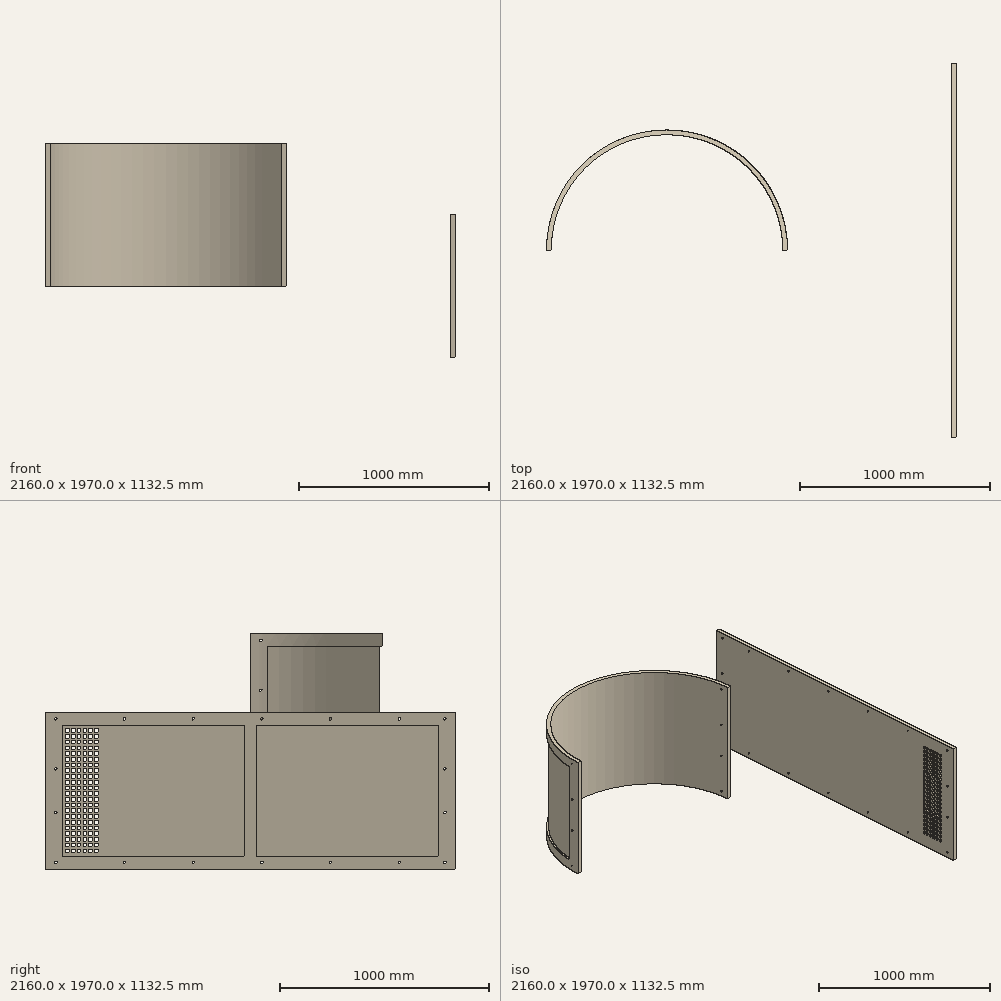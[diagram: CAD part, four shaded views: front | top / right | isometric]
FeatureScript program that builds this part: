
annotation { "Feature Type Name" : "Feature", "Feature Type Description" : "" }
export const myFeature = defineFeature(function(context is Context, id is Id, definition is map)
    precondition{}
    {
        {
            var Q0;
            Q0=qCreatedBy(makeId("Top.planeOp"),FACE);
            var sketch = newSketch(context, id + "F0", { "sketchPlane" : qUnion([Q0])});
            skArc(sketch, "E0", {"start": v(635, 0) * mm, "mid": v(0, 635) * mm, "end": v(-635, 0) * mm});
            skArc(sketch, "E1", {"start": v(610, 0) * mm, "mid": v(0, 610) * mm, "end": v(-610, 0) * mm});
            skLineSegment(sketch, "E2", {"start": v(-635, 0) * mm, "end": v(-610, 0) * mm});
            skLineSegment(sketch, "E3", {"start": v(610, 0) * mm, "end": v(635, 0) * mm});
            skSolve(sketch);
        }
        {
            var Q0;
            Q0 = qSketchRegion(id + "F0", true);
            extrude(context, id + "F1", {"entities" : qUnion([Q0]), "depth" : 755 * mm, "offsetDistance" : 25 * mm});
        }
        {
            var Q0;
            Q0=qCreatedBy(makeId("Top.planeOp"),FACE);
            cPlane(context, id + "F2", {"entities" : qUnion([Q0]), "cplaneType" : CPlaneType.OFFSET, "offset" : 62 * mm, "width" : 150 * mm, "height" : 150 * mm});
        }
        {
            var Q0;
            Q0=qCreatedBy(id+"F2.planeOp",FACE);
            var sketch = newSketch(context, id + "F3", { "sketchPlane" : qUnion([Q0])});
            skArc(sketch, "E4", {"start": v(629.97, 79.79) * mm, "mid": v(0, 635) * mm, "end": v(-629.97, 79.79) * mm});
            skArc(sketch, "E5", {"start": v(617.57, 78.22) * mm, "mid": v(0, 622.5) * mm, "end": v(-617.57, 78.22) * mm});
            skLineSegment(sketch, "E6", {"start": v(-629.97, 79.79) * mm, "end": v(-617.57, 78.22) * mm});
            skLineSegment(sketch, "E7", {"start": v(617.57, 78.22) * mm, "end": v(629.97, 79.79) * mm});
            skSolve(sketch);
        }
        {
            var Q0;
            Q0 = qSketchRegion(id + "F3", true);
            extrude(context, id + "F4", {"entities" : qUnion([Q0]), "operationType" : NewBodyOperationType.REMOVE, "depth" : 631 * mm, "offsetDistance" : 25 * mm});
        }
        {
            var Q0;
            Q0=qCreatedBy(makeId("Right.planeOp"),FACE);
            var sketch = newSketch(context, id + "F5", { "sketchPlane" : qUnion([Q0])});
            skCircle(sketch, "E8", {"center": v(50, 32.5) * mm, "radius": 6 * mm});
            skLineSegment(sketch, "E9", {"start": v(50, 32.5) * mm, "end": v(50, 272.5) * mm, "construction": true});
            skLineSegment(sketch, "E10", {"start": v(50, 272.5) * mm, "end": v(50, 482.5) * mm, "construction": true});
            skLineSegment(sketch, "E11", {"start": v(50, 482.5) * mm, "end": v(50, 722.5) * mm, "construction": true});
            skCircle(sketch, "E12", {"center": v(50, 722.5) * mm, "radius": 6 * mm});
            skCircle(sketch, "E13", {"center": v(50, 482.5) * mm, "radius": 6 * mm});
            skCircle(sketch, "E14", {"center": v(50, 272.5) * mm, "radius": 6 * mm});
            skSolve(sketch);
        }
        {
            var Q0;
            Q0 = qSketchRegion(id + "F5", true);
            extrude(context, id + "F6", {"entities" : qUnion([Q0]), "operationType" : NewBodyOperationType.REMOVE, "endBound" : BoundingType.THROUGH_ALL, "oppositeDirection" : true, "depth" : 25 * mm, "offsetDistance" : 25 * mm, "hasSecondDirection" : true, "secondDirectionBound" : BoundingType.THROUGH_ALL, "secondDirectionOppositeDirection" : false, "secondDirectionDepth" : 25 * mm});
        }
        {
            var Q0;
            Q0=qCreatedBy(makeId("Top.planeOp"),FACE);
            var sketch = newSketch(context, id + "F7", { "sketchPlane" : qUnion([Q0])});
            skArc(sketch, "E15", {"start": v(635, 0) * mm, "mid": v(109.45, 625.5) * mm, "end": v(-597.27, 215.62) * mm});
            skSolve(sketch);
        }
        {
            var Q0;
            Q0=qCreatedBy(makeId("Right.planeOp"),FACE);
            var sketch = newSketch(context, id + "F8", { "sketchPlane" : qUnion([Q0])});
            skCircle(sketch, "E16", {"center": v(50, 32.5) * mm, "radius": 6 * mm});
            skLineSegment(sketch, "E17", {"start": v(50, 32.5) * mm, "end": v(50, 722.5) * mm, "construction": true});
            skCircle(sketch, "E18", {"center": v(50, 722.5) * mm, "radius": 6 * mm});
            skSolve(sketch);
        }
        {
            var Q0;
            Q0 = qSketchRegion(id + "F8", true);
            extrude(context, id + "F9", {"entities" : qUnion([Q0]), "operationType" : NewBodyOperationType.REMOVE, "endBound" : BoundingType.THROUGH_ALL, "oppositeDirection" : true, "depth" : 25 * mm, "offsetDistance" : 25 * mm, "hasSecondDirection" : true, "secondDirectionBound" : BoundingType.THROUGH_ALL, "secondDirectionOppositeDirection" : false, "secondDirectionDepth" : 25 * mm});
        }
        {
            var Q0;
            Q0=qCreatedBy(makeId("Right.planeOp"),FACE);
            cPlane(context, id + "F10", {"entities" : qUnion([Q0]), "cplaneType" : CPlaneType.OFFSET, "offset" : 1500 * mm, "width" : 150 * mm, "height" : 150 * mm});
        }
        {
            var Q0;
            Q0=qCreatedBy(id+"F10.planeOp",FACE);
            var sketch = newSketch(context, id + "F11", { "sketchPlane" : qUnion([Q0])});
            skLineSegment(sketch, "E19.bottom", {"start": v(985, 377.5) * mm, "end": v(-985, 377.5) * mm});
            skLineSegment(sketch, "E19.top", {"start": v(985, -377.5) * mm, "end": v(-985, -377.5) * mm});
            skLineSegment(sketch, "E19.left", {"start": v(985, 377.5) * mm, "end": v(985, -377.5) * mm});
            skLineSegment(sketch, "E19.right", {"start": v(-985, 377.5) * mm, "end": v(-985, -377.5) * mm});
            skPoint(sketch, "E19.middle", {"position": v(0, 0) * mm});
            skCircle(sketch, "E20", {"center": v(-935, 345) * mm, "radius": 6 * mm});
            skCircle(sketch, "E21", {"center": v(-605, 345) * mm, "radius": 6 * mm});
            skCircle(sketch, "E22", {"center": v(-275, 345) * mm, "radius": 6 * mm});
            skCircle(sketch, "E23", {"center": v(55, 345) * mm, "radius": 6 * mm});
            skCircle(sketch, "E24", {"center": v(385, 345) * mm, "radius": 6 * mm});
            skCircle(sketch, "E25", {"center": v(715, 345) * mm, "radius": 6 * mm});
            skCircle(sketch, "E26", {"center": v(935, 345) * mm, "radius": 6 * mm});
            skCircle(sketch, "E27", {"center": v(-935, 105) * mm, "radius": 6 * mm});
            skCircle(sketch, "E28", {"center": v(-935, -105) * mm, "radius": 6 * mm});
            skCircle(sketch, "E29", {"center": v(-935, -345) * mm, "radius": 6 * mm});
            skCircle(sketch, "E30.MirrorC", {"center": v(-275, -345) * mm, "radius": 6 * mm});
            skCircle(sketch, "E31.MirrorC", {"center": v(715, -345) * mm, "radius": 6 * mm});
            skCircle(sketch, "E32.MirrorC", {"center": v(-605, -345) * mm, "radius": 6 * mm});
            skCircle(sketch, "E33.MirrorC", {"center": v(385, -345) * mm, "radius": 6 * mm});
            skCircle(sketch, "E34.MirrorC", {"center": v(55, -345) * mm, "radius": 6 * mm});
            skCircle(sketch, "E35.MirrorC", {"center": v(935, -105) * mm, "radius": 6 * mm});
            skCircle(sketch, "E36.MirrorC", {"center": v(935, 105) * mm, "radius": 6 * mm});
            skCircle(sketch, "E37", {"center": v(935, -345) * mm, "radius": 6 * mm});
            skSolve(sketch);
        }
        {
            var Q0;
            Q0 = qSketchRegion(id + "F11", true);
            extrude(context, id + "F12", {"entities" : qUnion([Q0]), "depth" : 25 * mm, "offsetDistance" : 25 * mm});
        }
        {
            var Q0;
            Q0=makeQuery(id+"F12.opExtrude","CAP_FACE",FACE,{"disambiguationData":[OSD([sQuery(id+"F11.wireOp",EDGE,"E19.bottom"),sQuery(id+"F11.wireOp",EDGE,"E19.left"),sQuery(id+"F11.wireOp",EDGE,"E19.right"),sQuery(id+"F11.wireOp",EDGE,"E20"),sQuery(id+"F11.wireOp",EDGE,"E21"),sQuery(id+"F11.wireOp",EDGE,"E22"),sQuery(id+"F11.wireOp",EDGE,"E23"),sQuery(id+"F11.wireOp",EDGE,"E24"),sQuery(id+"F11.wireOp",EDGE,"E25"),sQuery(id+"F11.wireOp",EDGE,"E26"),sQuery(id+"F11.wireOp",EDGE,"E27"),sQuery(id+"F11.wireOp",EDGE,"E28"),sQuery(id+"F11.wireOp",EDGE,"E29"),sQuery(id+"F11.wireOp",EDGE,"E30.MirrorC"),sQuery(id+"F11.wireOp",EDGE,"E31.MirrorC"),sQuery(id+"F11.wireOp",EDGE,"E32.MirrorC"),sQuery(id+"F11.wireOp",EDGE,"E33.MirrorC"),sQuery(id+"F11.wireOp",EDGE,"E34.MirrorC"),sQuery(id+"F11.wireOp",EDGE,"E19.top"),sQuery(id+"F11.wireOp",EDGE,"E35.MirrorC"),sQuery(id+"F11.wireOp",EDGE,"E36.MirrorC")])],"isStart":false});
            var sketch = newSketch(context, id + "F13", { "sketchPlane" : qUnion([Q0])});
            skLineSegment(sketch, "E38.left", {"start": v(905, 315.5) * mm, "end": v(905, -315.5) * mm});
            skLineSegment(sketch, "E38.right", {"start": v(-905, 315.5) * mm, "end": v(-905, -315.5) * mm});
            skPoint(sketch, "E38.middle", {"position": v(0, 0) * mm});
            skLineSegment(sketch, "E39", {"start": v(30, 315.5) * mm, "end": v(30, -315.5) * mm});
            skLineSegment(sketch, "E40", {"start": v(-30, 315.5) * mm, "end": v(-30, -315.5) * mm});
            skLineSegment(sketch, "E41", {"start": v(-905, -315.5) * mm, "end": v(-30, -315.5) * mm});
            skLineSegment(sketch, "E42", {"start": v(30, -315.5) * mm, "end": v(905, -315.5) * mm});
            skLineSegment(sketch, "E43", {"start": v(30, 315.5) * mm, "end": v(905, 315.5) * mm});
            skLineSegment(sketch, "E44", {"start": v(-905, 315.5) * mm, "end": v(-30, 315.5) * mm});
            skSolve(sketch);
        }
        {
            var Q0;
            Q0 = qSketchRegion(id + "F13", true);
            extrude(context, id + "F14", {"entities" : qUnion([Q0]), "operationType" : NewBodyOperationType.REMOVE, "oppositeDirection" : true, "depth" : 12.5 * mm, "offsetDistance" : 25 * mm});
        }
        {
            var Q0;
            Q0=makeQuery(id+"F14.boolean.opBoolean","COPY",FACE,{"derivedFrom":makeQuery(id+"F14.opExtrude","CAP_FACE",FACE,{"disambiguationData":[OSD([sQuery(id+"F13.wireOp",EDGE,"E38.right"),sQuery(id+"F13.wireOp",EDGE,"E40"),sQuery(id+"F13.wireOp",EDGE,"E41"),sQuery(id+"F13.wireOp",EDGE,"E44")])],"isStart":false})});
            var sketch = newSketch(context, id + "F15", { "sketchPlane" : qUnion([Q0])});
            skLineSegment(sketch, "E45.bottom", {"start": v(-887, 297.5) * mm, "end": v(-869.5, 297.5) * mm});
            skLineSegment(sketch, "E45.top", {"start": v(-887, 280) * mm, "end": v(-869.5, 280) * mm});
            skLineSegment(sketch, "E45.left", {"start": v(-887, 297.5) * mm, "end": v(-887, 280) * mm});
            skLineSegment(sketch, "E45.right", {"start": v(-869.5, 297.5) * mm, "end": v(-869.5, 280) * mm});
            skLineSegment(sketch, "E46.top", {"start": v(-887, 315.5) * mm, "end": v(-905, 315.5) * mm});
            skLineSegment(sketch, "E46.left", {"start": v(-887, 297.5) * mm, "end": v(-887, 315.5) * mm});
            skLineSegment(sketch, "E46.right", {"start": v(-905, 281.18) * mm, "end": v(-905, 315.5) * mm});
            skLineSegment(sketch, "E47.0.1.0", {"start": v(-869.5, 270) * mm, "end": v(-869.5, 252.5) * mm});
            skLineSegment(sketch, "E47.0.1.1", {"start": v(-887, 270) * mm, "end": v(-887, 288) * mm});
            skLineSegment(sketch, "E47.0.1.2", {"start": v(-887, 270) * mm, "end": v(-869.5, 270) * mm});
            skLineSegment(sketch, "E47.0.1.3", {"start": v(-887, 252.5) * mm, "end": v(-869.5, 252.5) * mm});
            skLineSegment(sketch, "E47.0.1.4", {"start": v(-887, 270) * mm, "end": v(-887, 252.5) * mm});
            skLineSegment(sketch, "E47.0.2.0", {"start": v(-869.5, 242.5) * mm, "end": v(-869.5, 225) * mm});
            skLineSegment(sketch, "E47.0.2.1", {"start": v(-887, 242.5) * mm, "end": v(-887, 260.5) * mm});
            skLineSegment(sketch, "E47.0.2.2", {"start": v(-887, 242.5) * mm, "end": v(-869.5, 242.5) * mm});
            skLineSegment(sketch, "E47.0.2.3", {"start": v(-887, 225) * mm, "end": v(-869.5, 225) * mm});
            skLineSegment(sketch, "E47.0.2.4", {"start": v(-887, 242.5) * mm, "end": v(-887, 225) * mm});
            skLineSegment(sketch, "E47.0.3.0", {"start": v(-869.5, 215) * mm, "end": v(-869.5, 197.5) * mm});
            skLineSegment(sketch, "E47.0.3.1", {"start": v(-887, 215) * mm, "end": v(-887, 233) * mm});
            skLineSegment(sketch, "E47.0.3.2", {"start": v(-887, 215) * mm, "end": v(-869.5, 215) * mm});
            skLineSegment(sketch, "E47.0.3.3", {"start": v(-887, 197.5) * mm, "end": v(-869.5, 197.5) * mm});
            skLineSegment(sketch, "E47.0.3.4", {"start": v(-887, 215) * mm, "end": v(-887, 197.5) * mm});
            skLineSegment(sketch, "E47.0.4.0", {"start": v(-869.5, 187.5) * mm, "end": v(-869.5, 170) * mm});
            skLineSegment(sketch, "E47.0.4.1", {"start": v(-887, 187.5) * mm, "end": v(-887, 205.5) * mm});
            skLineSegment(sketch, "E47.0.4.2", {"start": v(-887, 187.5) * mm, "end": v(-869.5, 187.5) * mm});
            skLineSegment(sketch, "E47.0.4.3", {"start": v(-887, 170) * mm, "end": v(-869.5, 170) * mm});
            skLineSegment(sketch, "E47.0.4.4", {"start": v(-887, 187.5) * mm, "end": v(-887, 170) * mm});
            skLineSegment(sketch, "E47.0.5.0", {"start": v(-869.5, 160) * mm, "end": v(-869.5, 142.5) * mm});
            skLineSegment(sketch, "E47.0.5.1", {"start": v(-887, 160) * mm, "end": v(-887, 178) * mm});
            skLineSegment(sketch, "E47.0.5.2", {"start": v(-887, 160) * mm, "end": v(-869.5, 160) * mm});
            skLineSegment(sketch, "E47.0.5.3", {"start": v(-887, 142.5) * mm, "end": v(-869.5, 142.5) * mm});
            skLineSegment(sketch, "E47.0.5.4", {"start": v(-887, 160) * mm, "end": v(-887, 142.5) * mm});
            skLineSegment(sketch, "E47.1.0.0", {"start": v(-842, 297.5) * mm, "end": v(-842, 280) * mm});
            skLineSegment(sketch, "E47.1.0.1", {"start": v(-859.5, 297.5) * mm, "end": v(-859.5, 315.5) * mm});
            skLineSegment(sketch, "E47.1.0.2", {"start": v(-859.5, 297.5) * mm, "end": v(-842, 297.5) * mm});
            skLineSegment(sketch, "E47.1.0.3", {"start": v(-859.5, 280) * mm, "end": v(-842, 280) * mm});
            skLineSegment(sketch, "E47.1.0.4", {"start": v(-859.5, 297.5) * mm, "end": v(-859.5, 280) * mm});
            skLineSegment(sketch, "E47.1.1.0", {"start": v(-842, 270) * mm, "end": v(-842, 252.5) * mm});
            skLineSegment(sketch, "E47.1.1.1", {"start": v(-859.5, 270) * mm, "end": v(-859.5, 288) * mm});
            skLineSegment(sketch, "E47.1.1.2", {"start": v(-859.5, 270) * mm, "end": v(-842, 270) * mm});
            skLineSegment(sketch, "E47.1.1.3", {"start": v(-859.5, 252.5) * mm, "end": v(-842, 252.5) * mm});
            skLineSegment(sketch, "E47.1.1.4", {"start": v(-859.5, 270) * mm, "end": v(-859.5, 252.5) * mm});
            skLineSegment(sketch, "E47.1.2.0", {"start": v(-842, 242.5) * mm, "end": v(-842, 225) * mm});
            skLineSegment(sketch, "E47.1.2.1", {"start": v(-859.5, 242.5) * mm, "end": v(-859.5, 260.5) * mm});
            skLineSegment(sketch, "E47.1.2.2", {"start": v(-859.5, 242.5) * mm, "end": v(-842, 242.5) * mm});
            skLineSegment(sketch, "E47.1.2.3", {"start": v(-859.5, 225) * mm, "end": v(-842, 225) * mm});
            skLineSegment(sketch, "E47.1.2.4", {"start": v(-859.5, 242.5) * mm, "end": v(-859.5, 225) * mm});
            skLineSegment(sketch, "E47.1.3.0", {"start": v(-842, 215) * mm, "end": v(-842, 197.5) * mm});
            skLineSegment(sketch, "E47.1.3.1", {"start": v(-859.5, 215) * mm, "end": v(-859.5, 233) * mm});
            skLineSegment(sketch, "E47.1.3.2", {"start": v(-859.5, 215) * mm, "end": v(-842, 215) * mm});
            skLineSegment(sketch, "E47.1.3.3", {"start": v(-859.5, 197.5) * mm, "end": v(-842, 197.5) * mm});
            skLineSegment(sketch, "E47.1.3.4", {"start": v(-859.5, 215) * mm, "end": v(-859.5, 197.5) * mm});
            skLineSegment(sketch, "E47.1.4.0", {"start": v(-842, 187.5) * mm, "end": v(-842, 170) * mm});
            skLineSegment(sketch, "E47.1.4.1", {"start": v(-859.5, 187.5) * mm, "end": v(-859.5, 205.5) * mm});
            skLineSegment(sketch, "E47.1.4.2", {"start": v(-859.5, 187.5) * mm, "end": v(-842, 187.5) * mm});
            skLineSegment(sketch, "E47.1.4.3", {"start": v(-859.5, 170) * mm, "end": v(-842, 170) * mm});
            skLineSegment(sketch, "E47.1.4.4", {"start": v(-859.5, 187.5) * mm, "end": v(-859.5, 170) * mm});
            skLineSegment(sketch, "E47.1.5.0", {"start": v(-842, 160) * mm, "end": v(-842, 142.5) * mm});
            skLineSegment(sketch, "E47.1.5.1", {"start": v(-859.5, 160) * mm, "end": v(-859.5, 178) * mm});
            skLineSegment(sketch, "E47.1.5.2", {"start": v(-859.5, 160) * mm, "end": v(-842, 160) * mm});
            skLineSegment(sketch, "E47.1.5.3", {"start": v(-859.5, 142.5) * mm, "end": v(-842, 142.5) * mm});
            skLineSegment(sketch, "E47.1.5.4", {"start": v(-859.5, 160) * mm, "end": v(-859.5, 142.5) * mm});
            skLineSegment(sketch, "E47.2.0.0", {"start": v(-814.5, 297.5) * mm, "end": v(-814.5, 280) * mm});
            skLineSegment(sketch, "E47.2.0.1", {"start": v(-832, 297.5) * mm, "end": v(-832, 315.5) * mm});
            skLineSegment(sketch, "E47.2.0.2", {"start": v(-832, 297.5) * mm, "end": v(-814.5, 297.5) * mm});
            skLineSegment(sketch, "E47.2.0.3", {"start": v(-832, 280) * mm, "end": v(-814.5, 280) * mm});
            skLineSegment(sketch, "E47.2.0.4", {"start": v(-832, 297.5) * mm, "end": v(-832, 280) * mm});
            skLineSegment(sketch, "E47.2.1.0", {"start": v(-814.5, 270) * mm, "end": v(-814.5, 252.5) * mm});
            skLineSegment(sketch, "E47.2.1.1", {"start": v(-832, 270) * mm, "end": v(-832, 288) * mm});
            skLineSegment(sketch, "E47.2.1.2", {"start": v(-832, 270) * mm, "end": v(-814.5, 270) * mm});
            skLineSegment(sketch, "E47.2.1.3", {"start": v(-832, 252.5) * mm, "end": v(-814.5, 252.5) * mm});
            skLineSegment(sketch, "E47.2.1.4", {"start": v(-832, 270) * mm, "end": v(-832, 252.5) * mm});
            skLineSegment(sketch, "E47.2.2.0", {"start": v(-814.5, 242.5) * mm, "end": v(-814.5, 225) * mm});
            skLineSegment(sketch, "E47.2.2.1", {"start": v(-832, 242.5) * mm, "end": v(-832, 260.5) * mm});
            skLineSegment(sketch, "E47.2.2.2", {"start": v(-832, 242.5) * mm, "end": v(-814.5, 242.5) * mm});
            skLineSegment(sketch, "E47.2.2.3", {"start": v(-832, 225) * mm, "end": v(-814.5, 225) * mm});
            skLineSegment(sketch, "E47.2.2.4", {"start": v(-832, 242.5) * mm, "end": v(-832, 225) * mm});
            skLineSegment(sketch, "E47.2.3.0", {"start": v(-814.5, 215) * mm, "end": v(-814.5, 197.5) * mm});
            skLineSegment(sketch, "E47.2.3.1", {"start": v(-832, 215) * mm, "end": v(-832, 233) * mm});
            skLineSegment(sketch, "E47.2.3.2", {"start": v(-832, 215) * mm, "end": v(-814.5, 215) * mm});
            skLineSegment(sketch, "E47.2.3.3", {"start": v(-832, 197.5) * mm, "end": v(-814.5, 197.5) * mm});
            skLineSegment(sketch, "E47.2.3.4", {"start": v(-832, 215) * mm, "end": v(-832, 197.5) * mm});
            skLineSegment(sketch, "E47.2.4.0", {"start": v(-814.5, 187.5) * mm, "end": v(-814.5, 170) * mm});
            skLineSegment(sketch, "E47.2.4.1", {"start": v(-832, 187.5) * mm, "end": v(-832, 205.5) * mm});
            skLineSegment(sketch, "E47.2.4.2", {"start": v(-832, 187.5) * mm, "end": v(-814.5, 187.5) * mm});
            skLineSegment(sketch, "E47.2.4.3", {"start": v(-832, 170) * mm, "end": v(-814.5, 170) * mm});
            skLineSegment(sketch, "E47.2.4.4", {"start": v(-832, 187.5) * mm, "end": v(-832, 170) * mm});
            skLineSegment(sketch, "E47.2.5.0", {"start": v(-814.5, 160) * mm, "end": v(-814.5, 142.5) * mm});
            skLineSegment(sketch, "E47.2.5.1", {"start": v(-832, 160) * mm, "end": v(-832, 178) * mm});
            skLineSegment(sketch, "E47.2.5.2", {"start": v(-832, 160) * mm, "end": v(-814.5, 160) * mm});
            skLineSegment(sketch, "E47.2.5.3", {"start": v(-832, 142.5) * mm, "end": v(-814.5, 142.5) * mm});
            skLineSegment(sketch, "E47.2.5.4", {"start": v(-832, 160) * mm, "end": v(-832, 142.5) * mm});
            skLineSegment(sketch, "E47.3.0.0", {"start": v(-787, 297.5) * mm, "end": v(-787, 280) * mm});
            skLineSegment(sketch, "E47.3.0.1", {"start": v(-804.5, 297.5) * mm, "end": v(-804.5, 315.5) * mm});
            skLineSegment(sketch, "E47.3.0.2", {"start": v(-804.5, 297.5) * mm, "end": v(-787, 297.5) * mm});
            skLineSegment(sketch, "E47.3.0.3", {"start": v(-804.5, 280) * mm, "end": v(-787, 280) * mm});
            skLineSegment(sketch, "E47.3.0.4", {"start": v(-804.5, 297.5) * mm, "end": v(-804.5, 280) * mm});
            skLineSegment(sketch, "E47.3.1.0", {"start": v(-787, 270) * mm, "end": v(-787, 252.5) * mm});
            skLineSegment(sketch, "E47.3.1.1", {"start": v(-804.5, 270) * mm, "end": v(-804.5, 288) * mm});
            skLineSegment(sketch, "E47.3.1.2", {"start": v(-804.5, 270) * mm, "end": v(-787, 270) * mm});
            skLineSegment(sketch, "E47.3.1.3", {"start": v(-804.5, 252.5) * mm, "end": v(-787, 252.5) * mm});
            skLineSegment(sketch, "E47.3.1.4", {"start": v(-804.5, 270) * mm, "end": v(-804.5, 252.5) * mm});
            skLineSegment(sketch, "E47.3.2.0", {"start": v(-787, 242.5) * mm, "end": v(-787, 225) * mm});
            skLineSegment(sketch, "E47.3.2.1", {"start": v(-804.5, 242.5) * mm, "end": v(-804.5, 260.5) * mm});
            skLineSegment(sketch, "E47.3.2.2", {"start": v(-804.5, 242.5) * mm, "end": v(-787, 242.5) * mm});
            skLineSegment(sketch, "E47.3.2.3", {"start": v(-804.5, 225) * mm, "end": v(-787, 225) * mm});
            skLineSegment(sketch, "E47.3.2.4", {"start": v(-804.5, 242.5) * mm, "end": v(-804.5, 225) * mm});
            skLineSegment(sketch, "E47.3.3.0", {"start": v(-787, 215) * mm, "end": v(-787, 197.5) * mm});
            skLineSegment(sketch, "E47.3.3.1", {"start": v(-804.5, 215) * mm, "end": v(-804.5, 233) * mm});
            skLineSegment(sketch, "E47.3.3.2", {"start": v(-804.5, 215) * mm, "end": v(-787, 215) * mm});
            skLineSegment(sketch, "E47.3.3.3", {"start": v(-804.5, 197.5) * mm, "end": v(-787, 197.5) * mm});
            skLineSegment(sketch, "E47.3.3.4", {"start": v(-804.5, 215) * mm, "end": v(-804.5, 197.5) * mm});
            skLineSegment(sketch, "E47.3.4.0", {"start": v(-787, 187.5) * mm, "end": v(-787, 170) * mm});
            skLineSegment(sketch, "E47.3.4.1", {"start": v(-804.5, 187.5) * mm, "end": v(-804.5, 205.5) * mm});
            skLineSegment(sketch, "E47.3.4.2", {"start": v(-804.5, 187.5) * mm, "end": v(-787, 187.5) * mm});
            skLineSegment(sketch, "E47.3.4.3", {"start": v(-804.5, 170) * mm, "end": v(-787, 170) * mm});
            skLineSegment(sketch, "E47.3.4.4", {"start": v(-804.5, 187.5) * mm, "end": v(-804.5, 170) * mm});
            skLineSegment(sketch, "E47.3.5.0", {"start": v(-787, 160) * mm, "end": v(-787, 142.5) * mm});
            skLineSegment(sketch, "E47.3.5.1", {"start": v(-804.5, 160) * mm, "end": v(-804.5, 178) * mm});
            skLineSegment(sketch, "E47.3.5.2", {"start": v(-804.5, 160) * mm, "end": v(-787, 160) * mm});
            skLineSegment(sketch, "E47.3.5.3", {"start": v(-804.5, 142.5) * mm, "end": v(-787, 142.5) * mm});
            skLineSegment(sketch, "E47.3.5.4", {"start": v(-804.5, 160) * mm, "end": v(-804.5, 142.5) * mm});
            skLineSegment(sketch, "E47.4.0.0", {"start": v(-759.5, 297.5) * mm, "end": v(-759.5, 280) * mm});
            skLineSegment(sketch, "E47.4.0.1", {"start": v(-777, 297.5) * mm, "end": v(-777, 315.5) * mm});
            skLineSegment(sketch, "E47.4.0.2", {"start": v(-777, 297.5) * mm, "end": v(-759.5, 297.5) * mm});
            skLineSegment(sketch, "E47.4.0.3", {"start": v(-777, 280) * mm, "end": v(-759.5, 280) * mm});
            skLineSegment(sketch, "E47.4.0.4", {"start": v(-777, 297.5) * mm, "end": v(-777, 280) * mm});
            skLineSegment(sketch, "E47.4.1.0", {"start": v(-759.5, 270) * mm, "end": v(-759.5, 252.5) * mm});
            skLineSegment(sketch, "E47.4.1.1", {"start": v(-777, 270) * mm, "end": v(-777, 288) * mm});
            skLineSegment(sketch, "E47.4.1.2", {"start": v(-777, 270) * mm, "end": v(-759.5, 270) * mm});
            skLineSegment(sketch, "E47.4.1.3", {"start": v(-777, 252.5) * mm, "end": v(-759.5, 252.5) * mm});
            skLineSegment(sketch, "E47.4.1.4", {"start": v(-777, 270) * mm, "end": v(-777, 252.5) * mm});
            skLineSegment(sketch, "E47.4.2.0", {"start": v(-759.5, 242.5) * mm, "end": v(-759.5, 225) * mm});
            skLineSegment(sketch, "E47.4.2.1", {"start": v(-777, 242.5) * mm, "end": v(-777, 260.5) * mm});
            skLineSegment(sketch, "E47.4.2.2", {"start": v(-777, 242.5) * mm, "end": v(-759.5, 242.5) * mm});
            skLineSegment(sketch, "E47.4.2.3", {"start": v(-777, 225) * mm, "end": v(-759.5, 225) * mm});
            skLineSegment(sketch, "E47.4.2.4", {"start": v(-777, 242.5) * mm, "end": v(-777, 225) * mm});
            skLineSegment(sketch, "E47.4.3.0", {"start": v(-759.5, 215) * mm, "end": v(-759.5, 197.5) * mm});
            skLineSegment(sketch, "E47.4.3.1", {"start": v(-777, 215) * mm, "end": v(-777, 233) * mm});
            skLineSegment(sketch, "E47.4.3.2", {"start": v(-777, 215) * mm, "end": v(-759.5, 215) * mm});
            skLineSegment(sketch, "E47.4.3.3", {"start": v(-777, 197.5) * mm, "end": v(-759.5, 197.5) * mm});
            skLineSegment(sketch, "E47.4.3.4", {"start": v(-777, 215) * mm, "end": v(-777, 197.5) * mm});
            skLineSegment(sketch, "E47.4.4.0", {"start": v(-759.5, 187.5) * mm, "end": v(-759.5, 170) * mm});
            skLineSegment(sketch, "E47.4.4.1", {"start": v(-777, 187.5) * mm, "end": v(-777, 205.5) * mm});
            skLineSegment(sketch, "E47.4.4.2", {"start": v(-777, 187.5) * mm, "end": v(-759.5, 187.5) * mm});
            skLineSegment(sketch, "E47.4.4.3", {"start": v(-777, 170) * mm, "end": v(-759.5, 170) * mm});
            skLineSegment(sketch, "E47.4.4.4", {"start": v(-777, 187.5) * mm, "end": v(-777, 170) * mm});
            skLineSegment(sketch, "E47.4.5.0", {"start": v(-759.5, 160) * mm, "end": v(-759.5, 142.5) * mm});
            skLineSegment(sketch, "E47.4.5.1", {"start": v(-777, 160) * mm, "end": v(-777, 178) * mm});
            skLineSegment(sketch, "E47.4.5.2", {"start": v(-777, 160) * mm, "end": v(-759.5, 160) * mm});
            skLineSegment(sketch, "E47.4.5.3", {"start": v(-777, 142.5) * mm, "end": v(-759.5, 142.5) * mm});
            skLineSegment(sketch, "E47.4.5.4", {"start": v(-777, 160) * mm, "end": v(-777, 142.5) * mm});
            skLineSegment(sketch, "E47.5.0.0", {"start": v(-732, 297.5) * mm, "end": v(-732, 280) * mm});
            skLineSegment(sketch, "E47.5.0.1", {"start": v(-749.5, 297.5) * mm, "end": v(-749.5, 315.5) * mm});
            skLineSegment(sketch, "E47.5.0.2", {"start": v(-749.5, 297.5) * mm, "end": v(-732, 297.5) * mm});
            skLineSegment(sketch, "E47.5.0.3", {"start": v(-749.5, 280) * mm, "end": v(-732, 280) * mm});
            skLineSegment(sketch, "E47.5.0.4", {"start": v(-749.5, 297.5) * mm, "end": v(-749.5, 280) * mm});
            skLineSegment(sketch, "E47.5.1.0", {"start": v(-732, 270) * mm, "end": v(-732, 252.5) * mm});
            skLineSegment(sketch, "E47.5.1.1", {"start": v(-749.5, 270) * mm, "end": v(-749.5, 288) * mm});
            skLineSegment(sketch, "E47.5.1.2", {"start": v(-749.5, 270) * mm, "end": v(-732, 270) * mm});
            skLineSegment(sketch, "E47.5.1.3", {"start": v(-749.5, 252.5) * mm, "end": v(-732, 252.5) * mm});
            skLineSegment(sketch, "E47.5.1.4", {"start": v(-749.5, 270) * mm, "end": v(-749.5, 252.5) * mm});
            skLineSegment(sketch, "E47.5.2.0", {"start": v(-732, 242.5) * mm, "end": v(-732, 225) * mm});
            skLineSegment(sketch, "E47.5.2.1", {"start": v(-749.5, 242.5) * mm, "end": v(-749.5, 260.5) * mm});
            skLineSegment(sketch, "E47.5.2.2", {"start": v(-749.5, 242.5) * mm, "end": v(-732, 242.5) * mm});
            skLineSegment(sketch, "E47.5.2.3", {"start": v(-749.5, 225) * mm, "end": v(-732, 225) * mm});
            skLineSegment(sketch, "E47.5.2.4", {"start": v(-749.5, 242.5) * mm, "end": v(-749.5, 225) * mm});
            skLineSegment(sketch, "E47.5.3.0", {"start": v(-732, 215) * mm, "end": v(-732, 197.5) * mm});
            skLineSegment(sketch, "E47.5.3.1", {"start": v(-749.5, 215) * mm, "end": v(-749.5, 233) * mm});
            skLineSegment(sketch, "E47.5.3.2", {"start": v(-749.5, 215) * mm, "end": v(-732, 215) * mm});
            skLineSegment(sketch, "E47.5.3.3", {"start": v(-749.5, 197.5) * mm, "end": v(-732, 197.5) * mm});
            skLineSegment(sketch, "E47.5.3.4", {"start": v(-749.5, 215) * mm, "end": v(-749.5, 197.5) * mm});
            skLineSegment(sketch, "E47.5.4.0", {"start": v(-732, 187.5) * mm, "end": v(-732, 170) * mm});
            skLineSegment(sketch, "E47.5.4.1", {"start": v(-749.5, 187.5) * mm, "end": v(-749.5, 205.5) * mm});
            skLineSegment(sketch, "E47.5.4.2", {"start": v(-749.5, 187.5) * mm, "end": v(-732, 187.5) * mm});
            skLineSegment(sketch, "E47.5.4.3", {"start": v(-749.5, 170) * mm, "end": v(-732, 170) * mm});
            skLineSegment(sketch, "E47.5.4.4", {"start": v(-749.5, 187.5) * mm, "end": v(-749.5, 170) * mm});
            skLineSegment(sketch, "E47.5.5.0", {"start": v(-732, 160) * mm, "end": v(-732, 142.5) * mm});
            skLineSegment(sketch, "E47.5.5.1", {"start": v(-749.5, 160) * mm, "end": v(-749.5, 178) * mm});
            skLineSegment(sketch, "E47.5.5.2", {"start": v(-749.5, 160) * mm, "end": v(-732, 160) * mm});
            skLineSegment(sketch, "E47.5.5.3", {"start": v(-749.5, 142.5) * mm, "end": v(-732, 142.5) * mm});
            skLineSegment(sketch, "E47.5.5.4", {"start": v(-749.5, 160) * mm, "end": v(-749.5, 142.5) * mm});
            skLineSegment(sketch, "E47.direction1", {"start": v(-887, 280) * mm, "end": v(-859.5, 280) * mm, "construction": true});
            skLineSegment(sketch, "E47.direction2", {"start": v(-887, 280) * mm, "end": v(-887, 252.5) * mm, "construction": true});
            skLineSegment(sketch, "E48.0.0.6", {"start": v(-869.5, 132.5) * mm, "end": v(-869.5, 115) * mm});
            skLineSegment(sketch, "E48.3.0.6", {"start": v(-887, 132.5) * mm, "end": v(-887, 150.5) * mm});
            skLineSegment(sketch, "E48.6.0.6", {"start": v(-887, 132.5) * mm, "end": v(-869.5, 132.5) * mm});
            skLineSegment(sketch, "E48.9.0.6", {"start": v(-887, 115) * mm, "end": v(-869.5, 115) * mm});
            skLineSegment(sketch, "E48.12.0.6", {"start": v(-887, 132.5) * mm, "end": v(-887, 115) * mm});
            skLineSegment(sketch, "E48.0.0.7", {"start": v(-869.5, 105) * mm, "end": v(-869.5, 87.5) * mm});
            skLineSegment(sketch, "E48.3.0.7", {"start": v(-887, 105) * mm, "end": v(-887, 123) * mm});
            skLineSegment(sketch, "E48.6.0.7", {"start": v(-887, 105) * mm, "end": v(-869.5, 105) * mm});
            skLineSegment(sketch, "E48.9.0.7", {"start": v(-887, 87.5) * mm, "end": v(-869.5, 87.5) * mm});
            skLineSegment(sketch, "E48.12.0.7", {"start": v(-887, 105) * mm, "end": v(-887, 87.5) * mm});
            skLineSegment(sketch, "E48.0.0.8", {"start": v(-869.5, 77.5) * mm, "end": v(-869.5, 60) * mm});
            skLineSegment(sketch, "E48.3.0.8", {"start": v(-887, 77.5) * mm, "end": v(-887, 95.5) * mm});
            skLineSegment(sketch, "E48.6.0.8", {"start": v(-887, 77.5) * mm, "end": v(-869.5, 77.5) * mm});
            skLineSegment(sketch, "E48.9.0.8", {"start": v(-887, 60) * mm, "end": v(-869.5, 60) * mm});
            skLineSegment(sketch, "E48.12.0.8", {"start": v(-887, 77.5) * mm, "end": v(-887, 60) * mm});
            skLineSegment(sketch, "E48.0.0.9", {"start": v(-869.5, 50) * mm, "end": v(-869.5, 32.5) * mm});
            skLineSegment(sketch, "E48.3.0.9", {"start": v(-887, 50) * mm, "end": v(-887, 68) * mm});
            skLineSegment(sketch, "E48.6.0.9", {"start": v(-887, 50) * mm, "end": v(-869.5, 50) * mm});
            skLineSegment(sketch, "E48.9.0.9", {"start": v(-887, 32.5) * mm, "end": v(-869.5, 32.5) * mm});
            skLineSegment(sketch, "E48.12.0.9", {"start": v(-887, 50) * mm, "end": v(-887, 32.5) * mm});
            skLineSegment(sketch, "E48.0.0.10", {"start": v(-869.5, 22.5) * mm, "end": v(-869.5, 5) * mm});
            skLineSegment(sketch, "E48.3.0.10", {"start": v(-887, 22.5) * mm, "end": v(-887, 40.5) * mm});
            skLineSegment(sketch, "E48.6.0.10", {"start": v(-887, 22.5) * mm, "end": v(-869.5, 22.5) * mm});
            skLineSegment(sketch, "E48.9.0.10", {"start": v(-887, 5) * mm, "end": v(-869.5, 5) * mm});
            skLineSegment(sketch, "E48.12.0.10", {"start": v(-887, 22.5) * mm, "end": v(-887, 5) * mm});
            skLineSegment(sketch, "E48.0.0.11", {"start": v(-869.5, -5) * mm, "end": v(-869.5, -22.5) * mm});
            skLineSegment(sketch, "E48.3.0.11", {"start": v(-887, -5) * mm, "end": v(-887, 13) * mm});
            skLineSegment(sketch, "E48.6.0.11", {"start": v(-887, -5) * mm, "end": v(-869.5, -5) * mm});
            skLineSegment(sketch, "E48.9.0.11", {"start": v(-887, -22.5) * mm, "end": v(-869.5, -22.5) * mm});
            skLineSegment(sketch, "E48.12.0.11", {"start": v(-887, -5) * mm, "end": v(-887, -22.5) * mm});
            skLineSegment(sketch, "E48.0.0.12", {"start": v(-869.5, -32.5) * mm, "end": v(-869.5, -50) * mm});
            skLineSegment(sketch, "E48.3.0.12", {"start": v(-887, -32.5) * mm, "end": v(-887, -14.5) * mm});
            skLineSegment(sketch, "E48.6.0.12", {"start": v(-887, -32.5) * mm, "end": v(-869.5, -32.5) * mm});
            skLineSegment(sketch, "E48.9.0.12", {"start": v(-887, -50) * mm, "end": v(-869.5, -50) * mm});
            skLineSegment(sketch, "E48.12.0.12", {"start": v(-887, -32.5) * mm, "end": v(-887, -50) * mm});
            skLineSegment(sketch, "E48.0.0.13", {"start": v(-869.5, -60) * mm, "end": v(-869.5, -77.5) * mm});
            skLineSegment(sketch, "E48.3.0.13", {"start": v(-887, -60) * mm, "end": v(-887, -42) * mm});
            skLineSegment(sketch, "E48.6.0.13", {"start": v(-887, -60) * mm, "end": v(-869.5, -60) * mm});
            skLineSegment(sketch, "E48.9.0.13", {"start": v(-887, -77.5) * mm, "end": v(-869.5, -77.5) * mm});
            skLineSegment(sketch, "E48.12.0.13", {"start": v(-887, -60) * mm, "end": v(-887, -77.5) * mm});
            skLineSegment(sketch, "E48.0.0.14", {"start": v(-869.5, -87.5) * mm, "end": v(-869.5, -105) * mm});
            skLineSegment(sketch, "E48.3.0.14", {"start": v(-887, -87.5) * mm, "end": v(-887, -69.5) * mm});
            skLineSegment(sketch, "E48.6.0.14", {"start": v(-887, -87.5) * mm, "end": v(-869.5, -87.5) * mm});
            skLineSegment(sketch, "E48.9.0.14", {"start": v(-887, -105) * mm, "end": v(-869.5, -105) * mm});
            skLineSegment(sketch, "E48.12.0.14", {"start": v(-887, -87.5) * mm, "end": v(-887, -105) * mm});
            skLineSegment(sketch, "E48.0.0.15", {"start": v(-869.5, -115) * mm, "end": v(-869.5, -132.5) * mm});
            skLineSegment(sketch, "E48.3.0.15", {"start": v(-887, -115) * mm, "end": v(-887, -97) * mm});
            skLineSegment(sketch, "E48.6.0.15", {"start": v(-887, -115) * mm, "end": v(-869.5, -115) * mm});
            skLineSegment(sketch, "E48.9.0.15", {"start": v(-887, -132.5) * mm, "end": v(-869.5, -132.5) * mm});
            skLineSegment(sketch, "E48.12.0.15", {"start": v(-887, -115) * mm, "end": v(-887, -132.5) * mm});
            skLineSegment(sketch, "E48.0.0.16", {"start": v(-869.5, -142.5) * mm, "end": v(-869.5, -160) * mm});
            skLineSegment(sketch, "E48.3.0.16", {"start": v(-887, -142.5) * mm, "end": v(-887, -124.5) * mm});
            skLineSegment(sketch, "E48.6.0.16", {"start": v(-887, -142.5) * mm, "end": v(-869.5, -142.5) * mm});
            skLineSegment(sketch, "E48.9.0.16", {"start": v(-887, -160) * mm, "end": v(-869.5, -160) * mm});
            skLineSegment(sketch, "E48.12.0.16", {"start": v(-887, -142.5) * mm, "end": v(-887, -160) * mm});
            skLineSegment(sketch, "E48.0.0.17", {"start": v(-869.5, -170) * mm, "end": v(-869.5, -187.5) * mm});
            skLineSegment(sketch, "E48.3.0.17", {"start": v(-887, -170) * mm, "end": v(-887, -152) * mm});
            skLineSegment(sketch, "E48.6.0.17", {"start": v(-887, -170) * mm, "end": v(-869.5, -170) * mm});
            skLineSegment(sketch, "E48.9.0.17", {"start": v(-887, -187.5) * mm, "end": v(-869.5, -187.5) * mm});
            skLineSegment(sketch, "E48.12.0.17", {"start": v(-887, -170) * mm, "end": v(-887, -187.5) * mm});
            skLineSegment(sketch, "E48.0.0.18", {"start": v(-869.5, -197.5) * mm, "end": v(-869.5, -215) * mm});
            skLineSegment(sketch, "E48.3.0.18", {"start": v(-887, -197.5) * mm, "end": v(-887, -179.5) * mm});
            skLineSegment(sketch, "E48.6.0.18", {"start": v(-887, -197.5) * mm, "end": v(-869.5, -197.5) * mm});
            skLineSegment(sketch, "E48.9.0.18", {"start": v(-887, -215) * mm, "end": v(-869.5, -215) * mm});
            skLineSegment(sketch, "E48.12.0.18", {"start": v(-887, -197.5) * mm, "end": v(-887, -215) * mm});
            skLineSegment(sketch, "E48.0.0.19", {"start": v(-869.5, -225) * mm, "end": v(-869.5, -242.5) * mm});
            skLineSegment(sketch, "E48.3.0.19", {"start": v(-887, -225) * mm, "end": v(-887, -207) * mm});
            skLineSegment(sketch, "E48.6.0.19", {"start": v(-887, -225) * mm, "end": v(-869.5, -225) * mm});
            skLineSegment(sketch, "E48.9.0.19", {"start": v(-887, -242.5) * mm, "end": v(-869.5, -242.5) * mm});
            skLineSegment(sketch, "E48.12.0.19", {"start": v(-887, -225) * mm, "end": v(-887, -242.5) * mm});
            skLineSegment(sketch, "E48.0.0.20", {"start": v(-869.5, -252.5) * mm, "end": v(-869.5, -270) * mm});
            skLineSegment(sketch, "E48.3.0.20", {"start": v(-887, -252.5) * mm, "end": v(-887, -234.5) * mm});
            skLineSegment(sketch, "E48.6.0.20", {"start": v(-887, -252.5) * mm, "end": v(-869.5, -252.5) * mm});
            skLineSegment(sketch, "E48.9.0.20", {"start": v(-887, -270) * mm, "end": v(-869.5, -270) * mm});
            skLineSegment(sketch, "E48.12.0.20", {"start": v(-887, -252.5) * mm, "end": v(-887, -270) * mm});
            skLineSegment(sketch, "E48.0.0.21", {"start": v(-869.5, -280) * mm, "end": v(-869.5, -297.5) * mm});
            skLineSegment(sketch, "E48.3.0.21", {"start": v(-887, -280) * mm, "end": v(-887, -262) * mm});
            skLineSegment(sketch, "E48.6.0.21", {"start": v(-887, -280) * mm, "end": v(-869.5, -280) * mm});
            skLineSegment(sketch, "E48.9.0.21", {"start": v(-887, -297.5) * mm, "end": v(-869.5, -297.5) * mm});
            skLineSegment(sketch, "E48.12.0.21", {"start": v(-887, -280) * mm, "end": v(-887, -297.5) * mm});
            skLineSegment(sketch, "E48.0.1.6", {"start": v(-842, 132.5) * mm, "end": v(-842, 115) * mm});
            skLineSegment(sketch, "E48.3.1.6", {"start": v(-859.5, 132.5) * mm, "end": v(-859.5, 150.5) * mm});
            skLineSegment(sketch, "E48.6.1.6", {"start": v(-859.5, 132.5) * mm, "end": v(-842, 132.5) * mm});
            skLineSegment(sketch, "E48.9.1.6", {"start": v(-859.5, 115) * mm, "end": v(-842, 115) * mm});
            skLineSegment(sketch, "E48.12.1.6", {"start": v(-859.5, 132.5) * mm, "end": v(-859.5, 115) * mm});
            skLineSegment(sketch, "E48.0.1.7", {"start": v(-842, 105) * mm, "end": v(-842, 87.5) * mm});
            skLineSegment(sketch, "E48.3.1.7", {"start": v(-859.5, 105) * mm, "end": v(-859.5, 123) * mm});
            skLineSegment(sketch, "E48.6.1.7", {"start": v(-859.5, 105) * mm, "end": v(-842, 105) * mm});
            skLineSegment(sketch, "E48.9.1.7", {"start": v(-859.5, 87.5) * mm, "end": v(-842, 87.5) * mm});
            skLineSegment(sketch, "E48.12.1.7", {"start": v(-859.5, 105) * mm, "end": v(-859.5, 87.5) * mm});
            skLineSegment(sketch, "E48.0.1.8", {"start": v(-842, 77.5) * mm, "end": v(-842, 60) * mm});
            skLineSegment(sketch, "E48.3.1.8", {"start": v(-859.5, 77.5) * mm, "end": v(-859.5, 95.5) * mm});
            skLineSegment(sketch, "E48.6.1.8", {"start": v(-859.5, 77.5) * mm, "end": v(-842, 77.5) * mm});
            skLineSegment(sketch, "E48.9.1.8", {"start": v(-859.5, 60) * mm, "end": v(-842, 60) * mm});
            skLineSegment(sketch, "E48.12.1.8", {"start": v(-859.5, 77.5) * mm, "end": v(-859.5, 60) * mm});
            skLineSegment(sketch, "E48.0.1.9", {"start": v(-842, 50) * mm, "end": v(-842, 32.5) * mm});
            skLineSegment(sketch, "E48.3.1.9", {"start": v(-859.5, 50) * mm, "end": v(-859.5, 68) * mm});
            skLineSegment(sketch, "E48.6.1.9", {"start": v(-859.5, 50) * mm, "end": v(-842, 50) * mm});
            skLineSegment(sketch, "E48.9.1.9", {"start": v(-859.5, 32.5) * mm, "end": v(-842, 32.5) * mm});
            skLineSegment(sketch, "E48.12.1.9", {"start": v(-859.5, 50) * mm, "end": v(-859.5, 32.5) * mm});
            skLineSegment(sketch, "E48.0.1.10", {"start": v(-842, 22.5) * mm, "end": v(-842, 5) * mm});
            skLineSegment(sketch, "E48.3.1.10", {"start": v(-859.5, 22.5) * mm, "end": v(-859.5, 40.5) * mm});
            skLineSegment(sketch, "E48.6.1.10", {"start": v(-859.5, 22.5) * mm, "end": v(-842, 22.5) * mm});
            skLineSegment(sketch, "E48.9.1.10", {"start": v(-859.5, 5) * mm, "end": v(-842, 5) * mm});
            skLineSegment(sketch, "E48.12.1.10", {"start": v(-859.5, 22.5) * mm, "end": v(-859.5, 5) * mm});
            skLineSegment(sketch, "E48.0.1.11", {"start": v(-842, -5) * mm, "end": v(-842, -22.5) * mm});
            skLineSegment(sketch, "E48.3.1.11", {"start": v(-859.5, -5) * mm, "end": v(-859.5, 13) * mm});
            skLineSegment(sketch, "E48.6.1.11", {"start": v(-859.5, -5) * mm, "end": v(-842, -5) * mm});
            skLineSegment(sketch, "E48.9.1.11", {"start": v(-859.5, -22.5) * mm, "end": v(-842, -22.5) * mm});
            skLineSegment(sketch, "E48.12.1.11", {"start": v(-859.5, -5) * mm, "end": v(-859.5, -22.5) * mm});
            skLineSegment(sketch, "E48.0.1.12", {"start": v(-842, -32.5) * mm, "end": v(-842, -50) * mm});
            skLineSegment(sketch, "E48.3.1.12", {"start": v(-859.5, -32.5) * mm, "end": v(-859.5, -14.5) * mm});
            skLineSegment(sketch, "E48.6.1.12", {"start": v(-859.5, -32.5) * mm, "end": v(-842, -32.5) * mm});
            skLineSegment(sketch, "E48.9.1.12", {"start": v(-859.5, -50) * mm, "end": v(-842, -50) * mm});
            skLineSegment(sketch, "E48.12.1.12", {"start": v(-859.5, -32.5) * mm, "end": v(-859.5, -50) * mm});
            skLineSegment(sketch, "E48.0.1.13", {"start": v(-842, -60) * mm, "end": v(-842, -77.5) * mm});
            skLineSegment(sketch, "E48.3.1.13", {"start": v(-859.5, -60) * mm, "end": v(-859.5, -42) * mm});
            skLineSegment(sketch, "E48.6.1.13", {"start": v(-859.5, -60) * mm, "end": v(-842, -60) * mm});
            skLineSegment(sketch, "E48.9.1.13", {"start": v(-859.5, -77.5) * mm, "end": v(-842, -77.5) * mm});
            skLineSegment(sketch, "E48.12.1.13", {"start": v(-859.5, -60) * mm, "end": v(-859.5, -77.5) * mm});
            skLineSegment(sketch, "E48.0.1.14", {"start": v(-842, -87.5) * mm, "end": v(-842, -105) * mm});
            skLineSegment(sketch, "E48.3.1.14", {"start": v(-859.5, -87.5) * mm, "end": v(-859.5, -69.5) * mm});
            skLineSegment(sketch, "E48.6.1.14", {"start": v(-859.5, -87.5) * mm, "end": v(-842, -87.5) * mm});
            skLineSegment(sketch, "E48.9.1.14", {"start": v(-859.5, -105) * mm, "end": v(-842, -105) * mm});
            skLineSegment(sketch, "E48.12.1.14", {"start": v(-859.5, -87.5) * mm, "end": v(-859.5, -105) * mm});
            skLineSegment(sketch, "E48.0.1.15", {"start": v(-842, -115) * mm, "end": v(-842, -132.5) * mm});
            skLineSegment(sketch, "E48.3.1.15", {"start": v(-859.5, -115) * mm, "end": v(-859.5, -97) * mm});
            skLineSegment(sketch, "E48.6.1.15", {"start": v(-859.5, -115) * mm, "end": v(-842, -115) * mm});
            skLineSegment(sketch, "E48.9.1.15", {"start": v(-859.5, -132.5) * mm, "end": v(-842, -132.5) * mm});
            skLineSegment(sketch, "E48.12.1.15", {"start": v(-859.5, -115) * mm, "end": v(-859.5, -132.5) * mm});
            skLineSegment(sketch, "E48.0.1.16", {"start": v(-842, -142.5) * mm, "end": v(-842, -160) * mm});
            skLineSegment(sketch, "E48.3.1.16", {"start": v(-859.5, -142.5) * mm, "end": v(-859.5, -124.5) * mm});
            skLineSegment(sketch, "E48.6.1.16", {"start": v(-859.5, -142.5) * mm, "end": v(-842, -142.5) * mm});
            skLineSegment(sketch, "E48.9.1.16", {"start": v(-859.5, -160) * mm, "end": v(-842, -160) * mm});
            skLineSegment(sketch, "E48.12.1.16", {"start": v(-859.5, -142.5) * mm, "end": v(-859.5, -160) * mm});
            skLineSegment(sketch, "E48.0.1.17", {"start": v(-842, -170) * mm, "end": v(-842, -187.5) * mm});
            skLineSegment(sketch, "E48.3.1.17", {"start": v(-859.5, -170) * mm, "end": v(-859.5, -152) * mm});
            skLineSegment(sketch, "E48.6.1.17", {"start": v(-859.5, -170) * mm, "end": v(-842, -170) * mm});
            skLineSegment(sketch, "E48.9.1.17", {"start": v(-859.5, -187.5) * mm, "end": v(-842, -187.5) * mm});
            skLineSegment(sketch, "E48.12.1.17", {"start": v(-859.5, -170) * mm, "end": v(-859.5, -187.5) * mm});
            skLineSegment(sketch, "E48.0.1.18", {"start": v(-842, -197.5) * mm, "end": v(-842, -215) * mm});
            skLineSegment(sketch, "E48.3.1.18", {"start": v(-859.5, -197.5) * mm, "end": v(-859.5, -179.5) * mm});
            skLineSegment(sketch, "E48.6.1.18", {"start": v(-859.5, -197.5) * mm, "end": v(-842, -197.5) * mm});
            skLineSegment(sketch, "E48.9.1.18", {"start": v(-859.5, -215) * mm, "end": v(-842, -215) * mm});
            skLineSegment(sketch, "E48.12.1.18", {"start": v(-859.5, -197.5) * mm, "end": v(-859.5, -215) * mm});
            skLineSegment(sketch, "E48.0.1.19", {"start": v(-842, -225) * mm, "end": v(-842, -242.5) * mm});
            skLineSegment(sketch, "E48.3.1.19", {"start": v(-859.5, -225) * mm, "end": v(-859.5, -207) * mm});
            skLineSegment(sketch, "E48.6.1.19", {"start": v(-859.5, -225) * mm, "end": v(-842, -225) * mm});
            skLineSegment(sketch, "E48.9.1.19", {"start": v(-859.5, -242.5) * mm, "end": v(-842, -242.5) * mm});
            skLineSegment(sketch, "E48.12.1.19", {"start": v(-859.5, -225) * mm, "end": v(-859.5, -242.5) * mm});
            skLineSegment(sketch, "E48.0.1.20", {"start": v(-842, -252.5) * mm, "end": v(-842, -270) * mm});
            skLineSegment(sketch, "E48.3.1.20", {"start": v(-859.5, -252.5) * mm, "end": v(-859.5, -234.5) * mm});
            skLineSegment(sketch, "E48.6.1.20", {"start": v(-859.5, -252.5) * mm, "end": v(-842, -252.5) * mm});
            skLineSegment(sketch, "E48.9.1.20", {"start": v(-859.5, -270) * mm, "end": v(-842, -270) * mm});
            skLineSegment(sketch, "E48.12.1.20", {"start": v(-859.5, -252.5) * mm, "end": v(-859.5, -270) * mm});
            skLineSegment(sketch, "E48.0.1.21", {"start": v(-842, -280) * mm, "end": v(-842, -297.5) * mm});
            skLineSegment(sketch, "E48.3.1.21", {"start": v(-859.5, -280) * mm, "end": v(-859.5, -262) * mm});
            skLineSegment(sketch, "E48.6.1.21", {"start": v(-859.5, -280) * mm, "end": v(-842, -280) * mm});
            skLineSegment(sketch, "E48.9.1.21", {"start": v(-859.5, -297.5) * mm, "end": v(-842, -297.5) * mm});
            skLineSegment(sketch, "E48.12.1.21", {"start": v(-859.5, -280) * mm, "end": v(-859.5, -297.5) * mm});
            skLineSegment(sketch, "E48.0.2.6", {"start": v(-814.5, 132.5) * mm, "end": v(-814.5, 115) * mm});
            skLineSegment(sketch, "E48.3.2.6", {"start": v(-832, 132.5) * mm, "end": v(-832, 150.5) * mm});
            skLineSegment(sketch, "E48.6.2.6", {"start": v(-832, 132.5) * mm, "end": v(-814.5, 132.5) * mm});
            skLineSegment(sketch, "E48.9.2.6", {"start": v(-832, 115) * mm, "end": v(-814.5, 115) * mm});
            skLineSegment(sketch, "E48.12.2.6", {"start": v(-832, 132.5) * mm, "end": v(-832, 115) * mm});
            skLineSegment(sketch, "E48.0.2.7", {"start": v(-814.5, 105) * mm, "end": v(-814.5, 87.5) * mm});
            skLineSegment(sketch, "E48.3.2.7", {"start": v(-832, 105) * mm, "end": v(-832, 123) * mm});
            skLineSegment(sketch, "E48.6.2.7", {"start": v(-832, 105) * mm, "end": v(-814.5, 105) * mm});
            skLineSegment(sketch, "E48.9.2.7", {"start": v(-832, 87.5) * mm, "end": v(-814.5, 87.5) * mm});
            skLineSegment(sketch, "E48.12.2.7", {"start": v(-832, 105) * mm, "end": v(-832, 87.5) * mm});
            skLineSegment(sketch, "E48.0.2.8", {"start": v(-814.5, 77.5) * mm, "end": v(-814.5, 60) * mm});
            skLineSegment(sketch, "E48.3.2.8", {"start": v(-832, 77.5) * mm, "end": v(-832, 95.5) * mm});
            skLineSegment(sketch, "E48.6.2.8", {"start": v(-832, 77.5) * mm, "end": v(-814.5, 77.5) * mm});
            skLineSegment(sketch, "E48.9.2.8", {"start": v(-832, 60) * mm, "end": v(-814.5, 60) * mm});
            skLineSegment(sketch, "E48.12.2.8", {"start": v(-832, 77.5) * mm, "end": v(-832, 60) * mm});
            skLineSegment(sketch, "E48.0.2.9", {"start": v(-814.5, 50) * mm, "end": v(-814.5, 32.5) * mm});
            skLineSegment(sketch, "E48.3.2.9", {"start": v(-832, 50) * mm, "end": v(-832, 68) * mm});
            skLineSegment(sketch, "E48.6.2.9", {"start": v(-832, 50) * mm, "end": v(-814.5, 50) * mm});
            skLineSegment(sketch, "E48.9.2.9", {"start": v(-832, 32.5) * mm, "end": v(-814.5, 32.5) * mm});
            skLineSegment(sketch, "E48.12.2.9", {"start": v(-832, 50) * mm, "end": v(-832, 32.5) * mm});
            skLineSegment(sketch, "E48.0.2.10", {"start": v(-814.5, 22.5) * mm, "end": v(-814.5, 5) * mm});
            skLineSegment(sketch, "E48.3.2.10", {"start": v(-832, 22.5) * mm, "end": v(-832, 40.5) * mm});
            skLineSegment(sketch, "E48.6.2.10", {"start": v(-832, 22.5) * mm, "end": v(-814.5, 22.5) * mm});
            skLineSegment(sketch, "E48.9.2.10", {"start": v(-832, 5) * mm, "end": v(-814.5, 5) * mm});
            skLineSegment(sketch, "E48.12.2.10", {"start": v(-832, 22.5) * mm, "end": v(-832, 5) * mm});
            skLineSegment(sketch, "E48.0.2.11", {"start": v(-814.5, -5) * mm, "end": v(-814.5, -22.5) * mm});
            skLineSegment(sketch, "E48.3.2.11", {"start": v(-832, -5) * mm, "end": v(-832, 13) * mm});
            skLineSegment(sketch, "E48.6.2.11", {"start": v(-832, -5) * mm, "end": v(-814.5, -5) * mm});
            skLineSegment(sketch, "E48.9.2.11", {"start": v(-832, -22.5) * mm, "end": v(-814.5, -22.5) * mm});
            skLineSegment(sketch, "E48.12.2.11", {"start": v(-832, -5) * mm, "end": v(-832, -22.5) * mm});
            skLineSegment(sketch, "E48.0.2.12", {"start": v(-814.5, -32.5) * mm, "end": v(-814.5, -50) * mm});
            skLineSegment(sketch, "E48.3.2.12", {"start": v(-832, -32.5) * mm, "end": v(-832, -14.5) * mm});
            skLineSegment(sketch, "E48.6.2.12", {"start": v(-832, -32.5) * mm, "end": v(-814.5, -32.5) * mm});
            skLineSegment(sketch, "E48.9.2.12", {"start": v(-832, -50) * mm, "end": v(-814.5, -50) * mm});
            skLineSegment(sketch, "E48.12.2.12", {"start": v(-832, -32.5) * mm, "end": v(-832, -50) * mm});
            skLineSegment(sketch, "E48.0.2.13", {"start": v(-814.5, -60) * mm, "end": v(-814.5, -77.5) * mm});
            skLineSegment(sketch, "E48.3.2.13", {"start": v(-832, -60) * mm, "end": v(-832, -42) * mm});
            skLineSegment(sketch, "E48.6.2.13", {"start": v(-832, -60) * mm, "end": v(-814.5, -60) * mm});
            skLineSegment(sketch, "E48.9.2.13", {"start": v(-832, -77.5) * mm, "end": v(-814.5, -77.5) * mm});
            skLineSegment(sketch, "E48.12.2.13", {"start": v(-832, -60) * mm, "end": v(-832, -77.5) * mm});
            skLineSegment(sketch, "E48.0.2.14", {"start": v(-814.5, -87.5) * mm, "end": v(-814.5, -105) * mm});
            skLineSegment(sketch, "E48.3.2.14", {"start": v(-832, -87.5) * mm, "end": v(-832, -69.5) * mm});
            skLineSegment(sketch, "E48.6.2.14", {"start": v(-832, -87.5) * mm, "end": v(-814.5, -87.5) * mm});
            skLineSegment(sketch, "E48.9.2.14", {"start": v(-832, -105) * mm, "end": v(-814.5, -105) * mm});
            skLineSegment(sketch, "E48.12.2.14", {"start": v(-832, -87.5) * mm, "end": v(-832, -105) * mm});
            skLineSegment(sketch, "E48.0.2.15", {"start": v(-814.5, -115) * mm, "end": v(-814.5, -132.5) * mm});
            skLineSegment(sketch, "E48.3.2.15", {"start": v(-832, -115) * mm, "end": v(-832, -97) * mm});
            skLineSegment(sketch, "E48.6.2.15", {"start": v(-832, -115) * mm, "end": v(-814.5, -115) * mm});
            skLineSegment(sketch, "E48.9.2.15", {"start": v(-832, -132.5) * mm, "end": v(-814.5, -132.5) * mm});
            skLineSegment(sketch, "E48.12.2.15", {"start": v(-832, -115) * mm, "end": v(-832, -132.5) * mm});
            skLineSegment(sketch, "E48.0.2.16", {"start": v(-814.5, -142.5) * mm, "end": v(-814.5, -160) * mm});
            skLineSegment(sketch, "E48.3.2.16", {"start": v(-832, -142.5) * mm, "end": v(-832, -124.5) * mm});
            skLineSegment(sketch, "E48.6.2.16", {"start": v(-832, -142.5) * mm, "end": v(-814.5, -142.5) * mm});
            skLineSegment(sketch, "E48.9.2.16", {"start": v(-832, -160) * mm, "end": v(-814.5, -160) * mm});
            skLineSegment(sketch, "E48.12.2.16", {"start": v(-832, -142.5) * mm, "end": v(-832, -160) * mm});
            skLineSegment(sketch, "E48.0.2.17", {"start": v(-814.5, -170) * mm, "end": v(-814.5, -187.5) * mm});
            skLineSegment(sketch, "E48.3.2.17", {"start": v(-832, -170) * mm, "end": v(-832, -152) * mm});
            skLineSegment(sketch, "E48.6.2.17", {"start": v(-832, -170) * mm, "end": v(-814.5, -170) * mm});
            skLineSegment(sketch, "E48.9.2.17", {"start": v(-832, -187.5) * mm, "end": v(-814.5, -187.5) * mm});
            skLineSegment(sketch, "E48.12.2.17", {"start": v(-832, -170) * mm, "end": v(-832, -187.5) * mm});
            skLineSegment(sketch, "E48.0.2.18", {"start": v(-814.5, -197.5) * mm, "end": v(-814.5, -215) * mm});
            skLineSegment(sketch, "E48.3.2.18", {"start": v(-832, -197.5) * mm, "end": v(-832, -179.5) * mm});
            skLineSegment(sketch, "E48.6.2.18", {"start": v(-832, -197.5) * mm, "end": v(-814.5, -197.5) * mm});
            skLineSegment(sketch, "E48.9.2.18", {"start": v(-832, -215) * mm, "end": v(-814.5, -215) * mm});
            skLineSegment(sketch, "E48.12.2.18", {"start": v(-832, -197.5) * mm, "end": v(-832, -215) * mm});
            skLineSegment(sketch, "E48.0.2.19", {"start": v(-814.5, -225) * mm, "end": v(-814.5, -242.5) * mm});
            skLineSegment(sketch, "E48.3.2.19", {"start": v(-832, -225) * mm, "end": v(-832, -207) * mm});
            skLineSegment(sketch, "E48.6.2.19", {"start": v(-832, -225) * mm, "end": v(-814.5, -225) * mm});
            skLineSegment(sketch, "E48.9.2.19", {"start": v(-832, -242.5) * mm, "end": v(-814.5, -242.5) * mm});
            skLineSegment(sketch, "E48.12.2.19", {"start": v(-832, -225) * mm, "end": v(-832, -242.5) * mm});
            skLineSegment(sketch, "E48.0.2.20", {"start": v(-814.5, -252.5) * mm, "end": v(-814.5, -270) * mm});
            skLineSegment(sketch, "E48.3.2.20", {"start": v(-832, -252.5) * mm, "end": v(-832, -234.5) * mm});
            skLineSegment(sketch, "E48.6.2.20", {"start": v(-832, -252.5) * mm, "end": v(-814.5, -252.5) * mm});
            skLineSegment(sketch, "E48.9.2.20", {"start": v(-832, -270) * mm, "end": v(-814.5, -270) * mm});
            skLineSegment(sketch, "E48.12.2.20", {"start": v(-832, -252.5) * mm, "end": v(-832, -270) * mm});
            skLineSegment(sketch, "E48.0.2.21", {"start": v(-814.5, -280) * mm, "end": v(-814.5, -297.5) * mm});
            skLineSegment(sketch, "E48.3.2.21", {"start": v(-832, -280) * mm, "end": v(-832, -262) * mm});
            skLineSegment(sketch, "E48.6.2.21", {"start": v(-832, -280) * mm, "end": v(-814.5, -280) * mm});
            skLineSegment(sketch, "E48.9.2.21", {"start": v(-832, -297.5) * mm, "end": v(-814.5, -297.5) * mm});
            skLineSegment(sketch, "E48.12.2.21", {"start": v(-832, -280) * mm, "end": v(-832, -297.5) * mm});
            skLineSegment(sketch, "E48.0.3.6", {"start": v(-787, 132.5) * mm, "end": v(-787, 115) * mm});
            skLineSegment(sketch, "E48.3.3.6", {"start": v(-804.5, 132.5) * mm, "end": v(-804.5, 150.5) * mm});
            skLineSegment(sketch, "E48.6.3.6", {"start": v(-804.5, 132.5) * mm, "end": v(-787, 132.5) * mm});
            skLineSegment(sketch, "E48.9.3.6", {"start": v(-804.5, 115) * mm, "end": v(-787, 115) * mm});
            skLineSegment(sketch, "E48.12.3.6", {"start": v(-804.5, 132.5) * mm, "end": v(-804.5, 115) * mm});
            skLineSegment(sketch, "E48.0.3.7", {"start": v(-787, 105) * mm, "end": v(-787, 87.5) * mm});
            skLineSegment(sketch, "E48.3.3.7", {"start": v(-804.5, 105) * mm, "end": v(-804.5, 123) * mm});
            skLineSegment(sketch, "E48.6.3.7", {"start": v(-804.5, 105) * mm, "end": v(-787, 105) * mm});
            skLineSegment(sketch, "E48.9.3.7", {"start": v(-804.5, 87.5) * mm, "end": v(-787, 87.5) * mm});
            skLineSegment(sketch, "E48.12.3.7", {"start": v(-804.5, 105) * mm, "end": v(-804.5, 87.5) * mm});
            skLineSegment(sketch, "E48.0.3.8", {"start": v(-787, 77.5) * mm, "end": v(-787, 60) * mm});
            skLineSegment(sketch, "E48.3.3.8", {"start": v(-804.5, 77.5) * mm, "end": v(-804.5, 95.5) * mm});
            skLineSegment(sketch, "E48.6.3.8", {"start": v(-804.5, 77.5) * mm, "end": v(-787, 77.5) * mm});
            skLineSegment(sketch, "E48.9.3.8", {"start": v(-804.5, 60) * mm, "end": v(-787, 60) * mm});
            skLineSegment(sketch, "E48.12.3.8", {"start": v(-804.5, 77.5) * mm, "end": v(-804.5, 60) * mm});
            skLineSegment(sketch, "E48.0.3.9", {"start": v(-787, 50) * mm, "end": v(-787, 32.5) * mm});
            skLineSegment(sketch, "E48.3.3.9", {"start": v(-804.5, 50) * mm, "end": v(-804.5, 68) * mm});
            skLineSegment(sketch, "E48.6.3.9", {"start": v(-804.5, 50) * mm, "end": v(-787, 50) * mm});
            skLineSegment(sketch, "E48.9.3.9", {"start": v(-804.5, 32.5) * mm, "end": v(-787, 32.5) * mm});
            skLineSegment(sketch, "E48.12.3.9", {"start": v(-804.5, 50) * mm, "end": v(-804.5, 32.5) * mm});
            skLineSegment(sketch, "E48.0.3.10", {"start": v(-787, 22.5) * mm, "end": v(-787, 5) * mm});
            skLineSegment(sketch, "E48.3.3.10", {"start": v(-804.5, 22.5) * mm, "end": v(-804.5, 40.5) * mm});
            skLineSegment(sketch, "E48.6.3.10", {"start": v(-804.5, 22.5) * mm, "end": v(-787, 22.5) * mm});
            skLineSegment(sketch, "E48.9.3.10", {"start": v(-804.5, 5) * mm, "end": v(-787, 5) * mm});
            skLineSegment(sketch, "E48.12.3.10", {"start": v(-804.5, 22.5) * mm, "end": v(-804.5, 5) * mm});
            skLineSegment(sketch, "E48.0.3.11", {"start": v(-787, -5) * mm, "end": v(-787, -22.5) * mm});
            skLineSegment(sketch, "E48.3.3.11", {"start": v(-804.5, -5) * mm, "end": v(-804.5, 13) * mm});
            skLineSegment(sketch, "E48.6.3.11", {"start": v(-804.5, -5) * mm, "end": v(-787, -5) * mm});
            skLineSegment(sketch, "E48.9.3.11", {"start": v(-804.5, -22.5) * mm, "end": v(-787, -22.5) * mm});
            skLineSegment(sketch, "E48.12.3.11", {"start": v(-804.5, -5) * mm, "end": v(-804.5, -22.5) * mm});
            skLineSegment(sketch, "E48.0.3.12", {"start": v(-787, -32.5) * mm, "end": v(-787, -50) * mm});
            skLineSegment(sketch, "E48.3.3.12", {"start": v(-804.5, -32.5) * mm, "end": v(-804.5, -14.5) * mm});
            skLineSegment(sketch, "E48.6.3.12", {"start": v(-804.5, -32.5) * mm, "end": v(-787, -32.5) * mm});
            skLineSegment(sketch, "E48.9.3.12", {"start": v(-804.5, -50) * mm, "end": v(-787, -50) * mm});
            skLineSegment(sketch, "E48.12.3.12", {"start": v(-804.5, -32.5) * mm, "end": v(-804.5, -50) * mm});
            skLineSegment(sketch, "E48.0.3.13", {"start": v(-787, -60) * mm, "end": v(-787, -77.5) * mm});
            skLineSegment(sketch, "E48.3.3.13", {"start": v(-804.5, -60) * mm, "end": v(-804.5, -42) * mm});
            skLineSegment(sketch, "E48.6.3.13", {"start": v(-804.5, -60) * mm, "end": v(-787, -60) * mm});
            skLineSegment(sketch, "E48.9.3.13", {"start": v(-804.5, -77.5) * mm, "end": v(-787, -77.5) * mm});
            skLineSegment(sketch, "E48.12.3.13", {"start": v(-804.5, -60) * mm, "end": v(-804.5, -77.5) * mm});
            skLineSegment(sketch, "E48.0.3.14", {"start": v(-787, -87.5) * mm, "end": v(-787, -105) * mm});
            skLineSegment(sketch, "E48.3.3.14", {"start": v(-804.5, -87.5) * mm, "end": v(-804.5, -69.5) * mm});
            skLineSegment(sketch, "E48.6.3.14", {"start": v(-804.5, -87.5) * mm, "end": v(-787, -87.5) * mm});
            skLineSegment(sketch, "E48.9.3.14", {"start": v(-804.5, -105) * mm, "end": v(-787, -105) * mm});
            skLineSegment(sketch, "E48.12.3.14", {"start": v(-804.5, -87.5) * mm, "end": v(-804.5, -105) * mm});
            skLineSegment(sketch, "E48.0.3.15", {"start": v(-787, -115) * mm, "end": v(-787, -132.5) * mm});
            skLineSegment(sketch, "E48.3.3.15", {"start": v(-804.5, -115) * mm, "end": v(-804.5, -97) * mm});
            skLineSegment(sketch, "E48.6.3.15", {"start": v(-804.5, -115) * mm, "end": v(-787, -115) * mm});
            skLineSegment(sketch, "E48.9.3.15", {"start": v(-804.5, -132.5) * mm, "end": v(-787, -132.5) * mm});
            skLineSegment(sketch, "E48.12.3.15", {"start": v(-804.5, -115) * mm, "end": v(-804.5, -132.5) * mm});
            skLineSegment(sketch, "E48.0.3.16", {"start": v(-787, -142.5) * mm, "end": v(-787, -160) * mm});
            skLineSegment(sketch, "E48.3.3.16", {"start": v(-804.5, -142.5) * mm, "end": v(-804.5, -124.5) * mm});
            skLineSegment(sketch, "E48.6.3.16", {"start": v(-804.5, -142.5) * mm, "end": v(-787, -142.5) * mm});
            skLineSegment(sketch, "E48.9.3.16", {"start": v(-804.5, -160) * mm, "end": v(-787, -160) * mm});
            skLineSegment(sketch, "E48.12.3.16", {"start": v(-804.5, -142.5) * mm, "end": v(-804.5, -160) * mm});
            skLineSegment(sketch, "E48.0.3.17", {"start": v(-787, -170) * mm, "end": v(-787, -187.5) * mm});
            skLineSegment(sketch, "E48.3.3.17", {"start": v(-804.5, -170) * mm, "end": v(-804.5, -152) * mm});
            skLineSegment(sketch, "E48.6.3.17", {"start": v(-804.5, -170) * mm, "end": v(-787, -170) * mm});
            skLineSegment(sketch, "E48.9.3.17", {"start": v(-804.5, -187.5) * mm, "end": v(-787, -187.5) * mm});
            skLineSegment(sketch, "E48.12.3.17", {"start": v(-804.5, -170) * mm, "end": v(-804.5, -187.5) * mm});
            skLineSegment(sketch, "E48.0.3.18", {"start": v(-787, -197.5) * mm, "end": v(-787, -215) * mm});
            skLineSegment(sketch, "E48.3.3.18", {"start": v(-804.5, -197.5) * mm, "end": v(-804.5, -179.5) * mm});
            skLineSegment(sketch, "E48.6.3.18", {"start": v(-804.5, -197.5) * mm, "end": v(-787, -197.5) * mm});
            skLineSegment(sketch, "E48.9.3.18", {"start": v(-804.5, -215) * mm, "end": v(-787, -215) * mm});
            skLineSegment(sketch, "E48.12.3.18", {"start": v(-804.5, -197.5) * mm, "end": v(-804.5, -215) * mm});
            skLineSegment(sketch, "E48.0.3.19", {"start": v(-787, -225) * mm, "end": v(-787, -242.5) * mm});
            skLineSegment(sketch, "E48.3.3.19", {"start": v(-804.5, -225) * mm, "end": v(-804.5, -207) * mm});
            skLineSegment(sketch, "E48.6.3.19", {"start": v(-804.5, -225) * mm, "end": v(-787, -225) * mm});
            skLineSegment(sketch, "E48.9.3.19", {"start": v(-804.5, -242.5) * mm, "end": v(-787, -242.5) * mm});
            skLineSegment(sketch, "E48.12.3.19", {"start": v(-804.5, -225) * mm, "end": v(-804.5, -242.5) * mm});
            skLineSegment(sketch, "E48.0.3.20", {"start": v(-787, -252.5) * mm, "end": v(-787, -270) * mm});
            skLineSegment(sketch, "E48.3.3.20", {"start": v(-804.5, -252.5) * mm, "end": v(-804.5, -234.5) * mm});
            skLineSegment(sketch, "E48.6.3.20", {"start": v(-804.5, -252.5) * mm, "end": v(-787, -252.5) * mm});
            skLineSegment(sketch, "E48.9.3.20", {"start": v(-804.5, -270) * mm, "end": v(-787, -270) * mm});
            skLineSegment(sketch, "E48.12.3.20", {"start": v(-804.5, -252.5) * mm, "end": v(-804.5, -270) * mm});
            skLineSegment(sketch, "E48.0.3.21", {"start": v(-787, -280) * mm, "end": v(-787, -297.5) * mm});
            skLineSegment(sketch, "E48.3.3.21", {"start": v(-804.5, -280) * mm, "end": v(-804.5, -262) * mm});
            skLineSegment(sketch, "E48.6.3.21", {"start": v(-804.5, -280) * mm, "end": v(-787, -280) * mm});
            skLineSegment(sketch, "E48.9.3.21", {"start": v(-804.5, -297.5) * mm, "end": v(-787, -297.5) * mm});
            skLineSegment(sketch, "E48.12.3.21", {"start": v(-804.5, -280) * mm, "end": v(-804.5, -297.5) * mm});
            skLineSegment(sketch, "E48.0.4.6", {"start": v(-759.5, 132.5) * mm, "end": v(-759.5, 115) * mm});
            skLineSegment(sketch, "E48.3.4.6", {"start": v(-777, 132.5) * mm, "end": v(-777, 150.5) * mm});
            skLineSegment(sketch, "E48.6.4.6", {"start": v(-777, 132.5) * mm, "end": v(-759.5, 132.5) * mm});
            skLineSegment(sketch, "E48.9.4.6", {"start": v(-777, 115) * mm, "end": v(-759.5, 115) * mm});
            skLineSegment(sketch, "E48.12.4.6", {"start": v(-777, 132.5) * mm, "end": v(-777, 115) * mm});
            skLineSegment(sketch, "E48.0.4.7", {"start": v(-759.5, 105) * mm, "end": v(-759.5, 87.5) * mm});
            skLineSegment(sketch, "E48.3.4.7", {"start": v(-777, 105) * mm, "end": v(-777, 123) * mm});
            skLineSegment(sketch, "E48.6.4.7", {"start": v(-777, 105) * mm, "end": v(-759.5, 105) * mm});
            skLineSegment(sketch, "E48.9.4.7", {"start": v(-777, 87.5) * mm, "end": v(-759.5, 87.5) * mm});
            skLineSegment(sketch, "E48.12.4.7", {"start": v(-777, 105) * mm, "end": v(-777, 87.5) * mm});
            skLineSegment(sketch, "E48.0.4.8", {"start": v(-759.5, 77.5) * mm, "end": v(-759.5, 60) * mm});
            skLineSegment(sketch, "E48.3.4.8", {"start": v(-777, 77.5) * mm, "end": v(-777, 95.5) * mm});
            skLineSegment(sketch, "E48.6.4.8", {"start": v(-777, 77.5) * mm, "end": v(-759.5, 77.5) * mm});
            skLineSegment(sketch, "E48.9.4.8", {"start": v(-777, 60) * mm, "end": v(-759.5, 60) * mm});
            skLineSegment(sketch, "E48.12.4.8", {"start": v(-777, 77.5) * mm, "end": v(-777, 60) * mm});
            skLineSegment(sketch, "E48.0.4.9", {"start": v(-759.5, 50) * mm, "end": v(-759.5, 32.5) * mm});
            skLineSegment(sketch, "E48.3.4.9", {"start": v(-777, 50) * mm, "end": v(-777, 68) * mm});
            skLineSegment(sketch, "E48.6.4.9", {"start": v(-777, 50) * mm, "end": v(-759.5, 50) * mm});
            skLineSegment(sketch, "E48.9.4.9", {"start": v(-777, 32.5) * mm, "end": v(-759.5, 32.5) * mm});
            skLineSegment(sketch, "E48.12.4.9", {"start": v(-777, 50) * mm, "end": v(-777, 32.5) * mm});
            skLineSegment(sketch, "E48.0.4.10", {"start": v(-759.5, 22.5) * mm, "end": v(-759.5, 5) * mm});
            skLineSegment(sketch, "E48.3.4.10", {"start": v(-777, 22.5) * mm, "end": v(-777, 40.5) * mm});
            skLineSegment(sketch, "E48.6.4.10", {"start": v(-777, 22.5) * mm, "end": v(-759.5, 22.5) * mm});
            skLineSegment(sketch, "E48.9.4.10", {"start": v(-777, 5) * mm, "end": v(-759.5, 5) * mm});
            skLineSegment(sketch, "E48.12.4.10", {"start": v(-777, 22.5) * mm, "end": v(-777, 5) * mm});
            skLineSegment(sketch, "E48.0.4.11", {"start": v(-759.5, -5) * mm, "end": v(-759.5, -22.5) * mm});
            skLineSegment(sketch, "E48.3.4.11", {"start": v(-777, -5) * mm, "end": v(-777, 13) * mm});
            skLineSegment(sketch, "E48.6.4.11", {"start": v(-777, -5) * mm, "end": v(-759.5, -5) * mm});
            skLineSegment(sketch, "E48.9.4.11", {"start": v(-777, -22.5) * mm, "end": v(-759.5, -22.5) * mm});
            skLineSegment(sketch, "E48.12.4.11", {"start": v(-777, -5) * mm, "end": v(-777, -22.5) * mm});
            skLineSegment(sketch, "E48.0.4.12", {"start": v(-759.5, -32.5) * mm, "end": v(-759.5, -50) * mm});
            skLineSegment(sketch, "E48.3.4.12", {"start": v(-777, -32.5) * mm, "end": v(-777, -14.5) * mm});
            skLineSegment(sketch, "E48.6.4.12", {"start": v(-777, -32.5) * mm, "end": v(-759.5, -32.5) * mm});
            skLineSegment(sketch, "E48.9.4.12", {"start": v(-777, -50) * mm, "end": v(-759.5, -50) * mm});
            skLineSegment(sketch, "E48.12.4.12", {"start": v(-777, -32.5) * mm, "end": v(-777, -50) * mm});
            skLineSegment(sketch, "E48.0.4.13", {"start": v(-759.5, -60) * mm, "end": v(-759.5, -77.5) * mm});
            skLineSegment(sketch, "E48.3.4.13", {"start": v(-777, -60) * mm, "end": v(-777, -42) * mm});
            skLineSegment(sketch, "E48.6.4.13", {"start": v(-777, -60) * mm, "end": v(-759.5, -60) * mm});
            skLineSegment(sketch, "E48.9.4.13", {"start": v(-777, -77.5) * mm, "end": v(-759.5, -77.5) * mm});
            skLineSegment(sketch, "E48.12.4.13", {"start": v(-777, -60) * mm, "end": v(-777, -77.5) * mm});
            skLineSegment(sketch, "E48.0.4.14", {"start": v(-759.5, -87.5) * mm, "end": v(-759.5, -105) * mm});
            skLineSegment(sketch, "E48.3.4.14", {"start": v(-777, -87.5) * mm, "end": v(-777, -69.5) * mm});
            skLineSegment(sketch, "E48.6.4.14", {"start": v(-777, -87.5) * mm, "end": v(-759.5, -87.5) * mm});
            skLineSegment(sketch, "E48.9.4.14", {"start": v(-777, -105) * mm, "end": v(-759.5, -105) * mm});
            skLineSegment(sketch, "E48.12.4.14", {"start": v(-777, -87.5) * mm, "end": v(-777, -105) * mm});
            skLineSegment(sketch, "E48.0.4.15", {"start": v(-759.5, -115) * mm, "end": v(-759.5, -132.5) * mm});
            skLineSegment(sketch, "E48.3.4.15", {"start": v(-777, -115) * mm, "end": v(-777, -97) * mm});
            skLineSegment(sketch, "E48.6.4.15", {"start": v(-777, -115) * mm, "end": v(-759.5, -115) * mm});
            skLineSegment(sketch, "E48.9.4.15", {"start": v(-777, -132.5) * mm, "end": v(-759.5, -132.5) * mm});
            skLineSegment(sketch, "E48.12.4.15", {"start": v(-777, -115) * mm, "end": v(-777, -132.5) * mm});
            skLineSegment(sketch, "E48.0.4.16", {"start": v(-759.5, -142.5) * mm, "end": v(-759.5, -160) * mm});
            skLineSegment(sketch, "E48.3.4.16", {"start": v(-777, -142.5) * mm, "end": v(-777, -124.5) * mm});
            skLineSegment(sketch, "E48.6.4.16", {"start": v(-777, -142.5) * mm, "end": v(-759.5, -142.5) * mm});
            skLineSegment(sketch, "E48.9.4.16", {"start": v(-777, -160) * mm, "end": v(-759.5, -160) * mm});
            skLineSegment(sketch, "E48.12.4.16", {"start": v(-777, -142.5) * mm, "end": v(-777, -160) * mm});
            skLineSegment(sketch, "E48.0.4.17", {"start": v(-759.5, -170) * mm, "end": v(-759.5, -187.5) * mm});
            skLineSegment(sketch, "E48.3.4.17", {"start": v(-777, -170) * mm, "end": v(-777, -152) * mm});
            skLineSegment(sketch, "E48.6.4.17", {"start": v(-777, -170) * mm, "end": v(-759.5, -170) * mm});
            skLineSegment(sketch, "E48.9.4.17", {"start": v(-777, -187.5) * mm, "end": v(-759.5, -187.5) * mm});
            skLineSegment(sketch, "E48.12.4.17", {"start": v(-777, -170) * mm, "end": v(-777, -187.5) * mm});
            skLineSegment(sketch, "E48.0.4.18", {"start": v(-759.5, -197.5) * mm, "end": v(-759.5, -215) * mm});
            skLineSegment(sketch, "E48.3.4.18", {"start": v(-777, -197.5) * mm, "end": v(-777, -179.5) * mm});
            skLineSegment(sketch, "E48.6.4.18", {"start": v(-777, -197.5) * mm, "end": v(-759.5, -197.5) * mm});
            skLineSegment(sketch, "E48.9.4.18", {"start": v(-777, -215) * mm, "end": v(-759.5, -215) * mm});
            skLineSegment(sketch, "E48.12.4.18", {"start": v(-777, -197.5) * mm, "end": v(-777, -215) * mm});
            skLineSegment(sketch, "E48.0.4.19", {"start": v(-759.5, -225) * mm, "end": v(-759.5, -242.5) * mm});
            skLineSegment(sketch, "E48.3.4.19", {"start": v(-777, -225) * mm, "end": v(-777, -207) * mm});
            skLineSegment(sketch, "E48.6.4.19", {"start": v(-777, -225) * mm, "end": v(-759.5, -225) * mm});
            skLineSegment(sketch, "E48.9.4.19", {"start": v(-777, -242.5) * mm, "end": v(-759.5, -242.5) * mm});
            skLineSegment(sketch, "E48.12.4.19", {"start": v(-777, -225) * mm, "end": v(-777, -242.5) * mm});
            skLineSegment(sketch, "E48.0.4.20", {"start": v(-759.5, -252.5) * mm, "end": v(-759.5, -270) * mm});
            skLineSegment(sketch, "E48.3.4.20", {"start": v(-777, -252.5) * mm, "end": v(-777, -234.5) * mm});
            skLineSegment(sketch, "E48.6.4.20", {"start": v(-777, -252.5) * mm, "end": v(-759.5, -252.5) * mm});
            skLineSegment(sketch, "E48.9.4.20", {"start": v(-777, -270) * mm, "end": v(-759.5, -270) * mm});
            skLineSegment(sketch, "E48.12.4.20", {"start": v(-777, -252.5) * mm, "end": v(-777, -270) * mm});
            skLineSegment(sketch, "E48.0.4.21", {"start": v(-759.5, -280) * mm, "end": v(-759.5, -297.5) * mm});
            skLineSegment(sketch, "E48.3.4.21", {"start": v(-777, -280) * mm, "end": v(-777, -262) * mm});
            skLineSegment(sketch, "E48.6.4.21", {"start": v(-777, -280) * mm, "end": v(-759.5, -280) * mm});
            skLineSegment(sketch, "E48.9.4.21", {"start": v(-777, -297.5) * mm, "end": v(-759.5, -297.5) * mm});
            skLineSegment(sketch, "E48.12.4.21", {"start": v(-777, -280) * mm, "end": v(-777, -297.5) * mm});
            skLineSegment(sketch, "E48.0.5.6", {"start": v(-732, 132.5) * mm, "end": v(-732, 115) * mm});
            skLineSegment(sketch, "E48.3.5.6", {"start": v(-749.5, 132.5) * mm, "end": v(-749.5, 150.5) * mm});
            skLineSegment(sketch, "E48.6.5.6", {"start": v(-749.5, 132.5) * mm, "end": v(-732, 132.5) * mm});
            skLineSegment(sketch, "E48.9.5.6", {"start": v(-749.5, 115) * mm, "end": v(-732, 115) * mm});
            skLineSegment(sketch, "E48.12.5.6", {"start": v(-749.5, 132.5) * mm, "end": v(-749.5, 115) * mm});
            skLineSegment(sketch, "E48.0.5.7", {"start": v(-732, 105) * mm, "end": v(-732, 87.5) * mm});
            skLineSegment(sketch, "E48.3.5.7", {"start": v(-749.5, 105) * mm, "end": v(-749.5, 123) * mm});
            skLineSegment(sketch, "E48.6.5.7", {"start": v(-749.5, 105) * mm, "end": v(-732, 105) * mm});
            skLineSegment(sketch, "E48.9.5.7", {"start": v(-749.5, 87.5) * mm, "end": v(-732, 87.5) * mm});
            skLineSegment(sketch, "E48.12.5.7", {"start": v(-749.5, 105) * mm, "end": v(-749.5, 87.5) * mm});
            skLineSegment(sketch, "E48.0.5.8", {"start": v(-732, 77.5) * mm, "end": v(-732, 60) * mm});
            skLineSegment(sketch, "E48.3.5.8", {"start": v(-749.5, 77.5) * mm, "end": v(-749.5, 95.5) * mm});
            skLineSegment(sketch, "E48.6.5.8", {"start": v(-749.5, 77.5) * mm, "end": v(-732, 77.5) * mm});
            skLineSegment(sketch, "E48.9.5.8", {"start": v(-749.5, 60) * mm, "end": v(-732, 60) * mm});
            skLineSegment(sketch, "E48.12.5.8", {"start": v(-749.5, 77.5) * mm, "end": v(-749.5, 60) * mm});
            skLineSegment(sketch, "E48.0.5.9", {"start": v(-732, 50) * mm, "end": v(-732, 32.5) * mm});
            skLineSegment(sketch, "E48.3.5.9", {"start": v(-749.5, 50) * mm, "end": v(-749.5, 68) * mm});
            skLineSegment(sketch, "E48.6.5.9", {"start": v(-749.5, 50) * mm, "end": v(-732, 50) * mm});
            skLineSegment(sketch, "E48.9.5.9", {"start": v(-749.5, 32.5) * mm, "end": v(-732, 32.5) * mm});
            skLineSegment(sketch, "E48.12.5.9", {"start": v(-749.5, 50) * mm, "end": v(-749.5, 32.5) * mm});
            skLineSegment(sketch, "E48.0.5.10", {"start": v(-732, 22.5) * mm, "end": v(-732, 5) * mm});
            skLineSegment(sketch, "E48.3.5.10", {"start": v(-749.5, 22.5) * mm, "end": v(-749.5, 40.5) * mm});
            skLineSegment(sketch, "E48.6.5.10", {"start": v(-749.5, 22.5) * mm, "end": v(-732, 22.5) * mm});
            skLineSegment(sketch, "E48.9.5.10", {"start": v(-749.5, 5) * mm, "end": v(-732, 5) * mm});
            skLineSegment(sketch, "E48.12.5.10", {"start": v(-749.5, 22.5) * mm, "end": v(-749.5, 5) * mm});
            skLineSegment(sketch, "E48.0.5.11", {"start": v(-732, -5) * mm, "end": v(-732, -22.5) * mm});
            skLineSegment(sketch, "E48.3.5.11", {"start": v(-749.5, -5) * mm, "end": v(-749.5, 13) * mm});
            skLineSegment(sketch, "E48.6.5.11", {"start": v(-749.5, -5) * mm, "end": v(-732, -5) * mm});
            skLineSegment(sketch, "E48.9.5.11", {"start": v(-749.5, -22.5) * mm, "end": v(-732, -22.5) * mm});
            skLineSegment(sketch, "E48.12.5.11", {"start": v(-749.5, -5) * mm, "end": v(-749.5, -22.5) * mm});
            skLineSegment(sketch, "E48.0.5.12", {"start": v(-732, -32.5) * mm, "end": v(-732, -50) * mm});
            skLineSegment(sketch, "E48.3.5.12", {"start": v(-749.5, -32.5) * mm, "end": v(-749.5, -14.5) * mm});
            skLineSegment(sketch, "E48.6.5.12", {"start": v(-749.5, -32.5) * mm, "end": v(-732, -32.5) * mm});
            skLineSegment(sketch, "E48.9.5.12", {"start": v(-749.5, -50) * mm, "end": v(-732, -50) * mm});
            skLineSegment(sketch, "E48.12.5.12", {"start": v(-749.5, -32.5) * mm, "end": v(-749.5, -50) * mm});
            skLineSegment(sketch, "E48.0.5.13", {"start": v(-732, -60) * mm, "end": v(-732, -77.5) * mm});
            skLineSegment(sketch, "E48.3.5.13", {"start": v(-749.5, -60) * mm, "end": v(-749.5, -42) * mm});
            skLineSegment(sketch, "E48.6.5.13", {"start": v(-749.5, -60) * mm, "end": v(-732, -60) * mm});
            skLineSegment(sketch, "E48.9.5.13", {"start": v(-749.5, -77.5) * mm, "end": v(-732, -77.5) * mm});
            skLineSegment(sketch, "E48.12.5.13", {"start": v(-749.5, -60) * mm, "end": v(-749.5, -77.5) * mm});
            skLineSegment(sketch, "E48.0.5.14", {"start": v(-732, -87.5) * mm, "end": v(-732, -105) * mm});
            skLineSegment(sketch, "E48.3.5.14", {"start": v(-749.5, -87.5) * mm, "end": v(-749.5, -69.5) * mm});
            skLineSegment(sketch, "E48.6.5.14", {"start": v(-749.5, -87.5) * mm, "end": v(-732, -87.5) * mm});
            skLineSegment(sketch, "E48.9.5.14", {"start": v(-749.5, -105) * mm, "end": v(-732, -105) * mm});
            skLineSegment(sketch, "E48.12.5.14", {"start": v(-749.5, -87.5) * mm, "end": v(-749.5, -105) * mm});
            skLineSegment(sketch, "E48.0.5.15", {"start": v(-732, -115) * mm, "end": v(-732, -132.5) * mm});
            skLineSegment(sketch, "E48.3.5.15", {"start": v(-749.5, -115) * mm, "end": v(-749.5, -97) * mm});
            skLineSegment(sketch, "E48.6.5.15", {"start": v(-749.5, -115) * mm, "end": v(-732, -115) * mm});
            skLineSegment(sketch, "E48.9.5.15", {"start": v(-749.5, -132.5) * mm, "end": v(-732, -132.5) * mm});
            skLineSegment(sketch, "E48.12.5.15", {"start": v(-749.5, -115) * mm, "end": v(-749.5, -132.5) * mm});
            skLineSegment(sketch, "E48.0.5.16", {"start": v(-732, -142.5) * mm, "end": v(-732, -160) * mm});
            skLineSegment(sketch, "E48.3.5.16", {"start": v(-749.5, -142.5) * mm, "end": v(-749.5, -124.5) * mm});
            skLineSegment(sketch, "E48.6.5.16", {"start": v(-749.5, -142.5) * mm, "end": v(-732, -142.5) * mm});
            skLineSegment(sketch, "E48.9.5.16", {"start": v(-749.5, -160) * mm, "end": v(-732, -160) * mm});
            skLineSegment(sketch, "E48.12.5.16", {"start": v(-749.5, -142.5) * mm, "end": v(-749.5, -160) * mm});
            skLineSegment(sketch, "E48.0.5.17", {"start": v(-732, -170) * mm, "end": v(-732, -187.5) * mm});
            skLineSegment(sketch, "E48.3.5.17", {"start": v(-749.5, -170) * mm, "end": v(-749.5, -152) * mm});
            skLineSegment(sketch, "E48.6.5.17", {"start": v(-749.5, -170) * mm, "end": v(-732, -170) * mm});
            skLineSegment(sketch, "E48.9.5.17", {"start": v(-749.5, -187.5) * mm, "end": v(-732, -187.5) * mm});
            skLineSegment(sketch, "E48.12.5.17", {"start": v(-749.5, -170) * mm, "end": v(-749.5, -187.5) * mm});
            skLineSegment(sketch, "E48.0.5.18", {"start": v(-732, -197.5) * mm, "end": v(-732, -215) * mm});
            skLineSegment(sketch, "E48.3.5.18", {"start": v(-749.5, -197.5) * mm, "end": v(-749.5, -179.5) * mm});
            skLineSegment(sketch, "E48.6.5.18", {"start": v(-749.5, -197.5) * mm, "end": v(-732, -197.5) * mm});
            skLineSegment(sketch, "E48.9.5.18", {"start": v(-749.5, -215) * mm, "end": v(-732, -215) * mm});
            skLineSegment(sketch, "E48.12.5.18", {"start": v(-749.5, -197.5) * mm, "end": v(-749.5, -215) * mm});
            skLineSegment(sketch, "E48.0.5.19", {"start": v(-732, -225) * mm, "end": v(-732, -242.5) * mm});
            skLineSegment(sketch, "E48.3.5.19", {"start": v(-749.5, -225) * mm, "end": v(-749.5, -207) * mm});
            skLineSegment(sketch, "E48.6.5.19", {"start": v(-749.5, -225) * mm, "end": v(-732, -225) * mm});
            skLineSegment(sketch, "E48.9.5.19", {"start": v(-749.5, -242.5) * mm, "end": v(-732, -242.5) * mm});
            skLineSegment(sketch, "E48.12.5.19", {"start": v(-749.5, -225) * mm, "end": v(-749.5, -242.5) * mm});
            skLineSegment(sketch, "E48.0.5.20", {"start": v(-732, -252.5) * mm, "end": v(-732, -270) * mm});
            skLineSegment(sketch, "E48.3.5.20", {"start": v(-749.5, -252.5) * mm, "end": v(-749.5, -234.5) * mm});
            skLineSegment(sketch, "E48.6.5.20", {"start": v(-749.5, -252.5) * mm, "end": v(-732, -252.5) * mm});
            skLineSegment(sketch, "E48.9.5.20", {"start": v(-749.5, -270) * mm, "end": v(-732, -270) * mm});
            skLineSegment(sketch, "E48.12.5.20", {"start": v(-749.5, -252.5) * mm, "end": v(-749.5, -270) * mm});
            skLineSegment(sketch, "E48.0.5.21", {"start": v(-732, -280) * mm, "end": v(-732, -297.5) * mm});
            skLineSegment(sketch, "E48.3.5.21", {"start": v(-749.5, -280) * mm, "end": v(-749.5, -262) * mm});
            skLineSegment(sketch, "E48.6.5.21", {"start": v(-749.5, -280) * mm, "end": v(-732, -280) * mm});
            skLineSegment(sketch, "E48.9.5.21", {"start": v(-749.5, -297.5) * mm, "end": v(-732, -297.5) * mm});
            skLineSegment(sketch, "E48.12.5.21", {"start": v(-749.5, -280) * mm, "end": v(-749.5, -297.5) * mm});
            skSolve(sketch);
        }
        {
            var Q0;
            Q0 = qSketchRegion(id + "F15", true);
            extrude(context, id + "F16", {"entities" : qUnion([Q0]), "operationType" : NewBodyOperationType.REMOVE, "oppositeDirection" : true, "depth" : 25 * mm, "offsetDistance" : 25 * mm});
        }
    });
